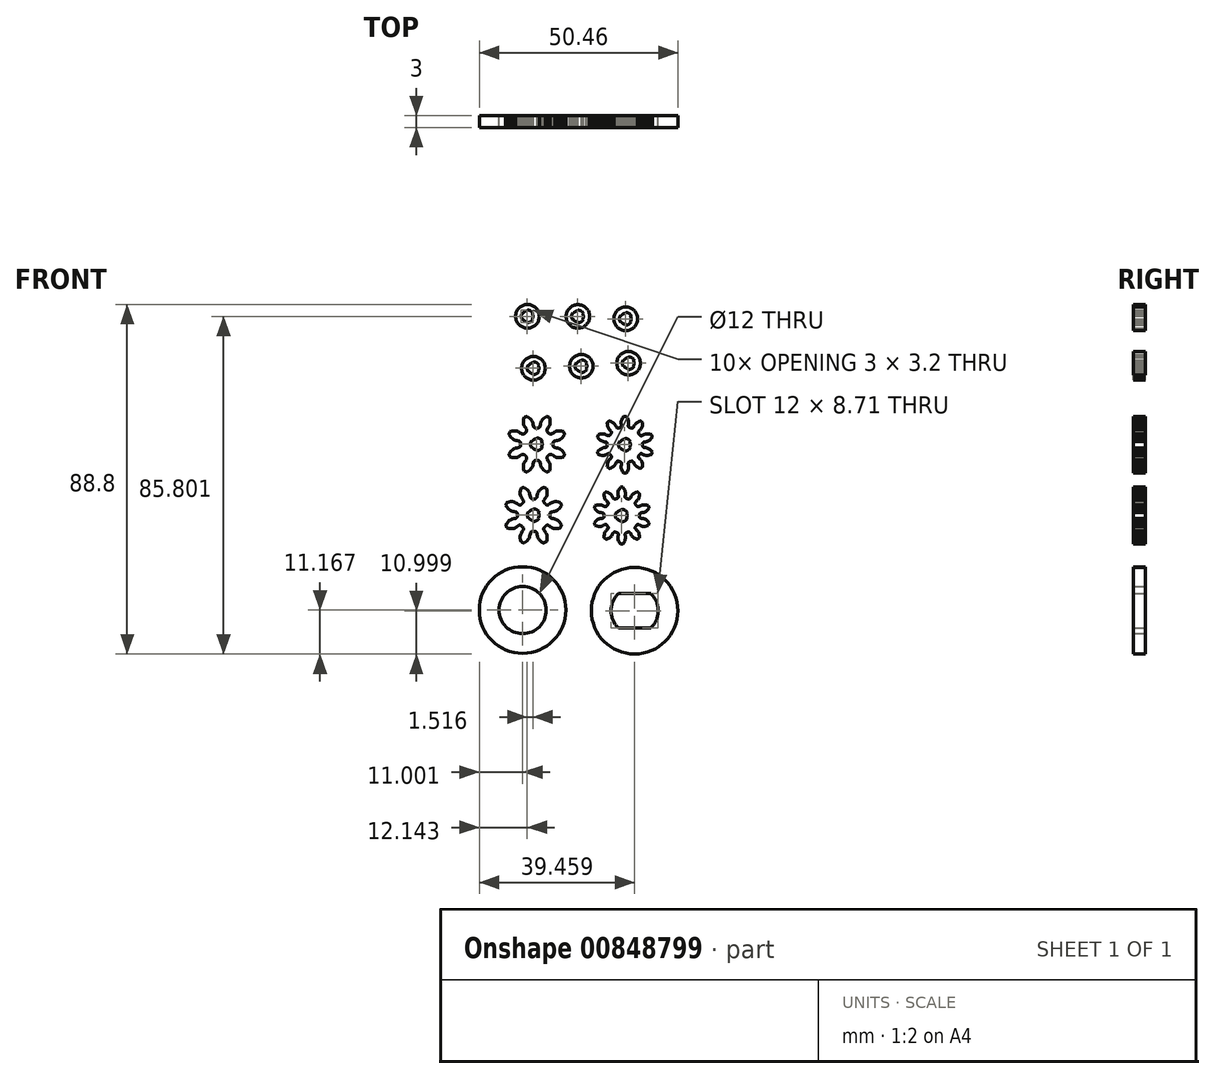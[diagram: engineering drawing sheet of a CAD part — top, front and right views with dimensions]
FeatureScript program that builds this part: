
annotation { "Feature Type Name" : "Feature", "Feature Type Description" : "" }
export const myFeature = defineFeature(function(context is Context, id is Id, definition is map)
    precondition{}
    {
        {
            var Q0;
            Q0=qCreatedBy(makeId("Front.planeOp"),FACE);
            var sketch = newSketch(context, id + "F0", { "sketchPlane" : qUnion([Q0])});
            skArc(sketch, "E0", {"start": v(10.6, 41.57) * mm, "mid": v(10.38, 40.77) * mm, "end": v(10.6, 39.97) * mm});
            skArc(sketch, "E1", {"start": v(13.36, 41.57) * mm, "mid": v(12.78, 42.16) * mm, "end": v(11.98, 42.37) * mm});
            skArc(sketch, "E2", {"start": v(13.2, 40.07) * mm, "mid": v(13.38, 40.77) * mm, "end": v(13.2, 41.47) * mm});
            skArc(sketch, "E3", {"start": v(10.77, 40.07) * mm, "mid": v(11.28, 39.56) * mm, "end": v(11.98, 39.37) * mm});
            skLineSegment(sketch, "E4", {"start": v(13.2, 41.47) * mm, "end": v(13.36, 41.57) * mm});
            skLineSegment(sketch, "E5", {"start": v(13.2, 40.07) * mm, "end": v(13.36, 39.97) * mm});
            skLineSegment(sketch, "E6", {"start": v(11.98, 39.37) * mm, "end": v(11.98, 39.17) * mm});
            skLineSegment(sketch, "E7", {"start": v(10.77, 40.07) * mm, "end": v(10.6, 39.97) * mm});
            skLineSegment(sketch, "E8", {"start": v(10.77, 41.47) * mm, "end": v(10.6, 41.57) * mm});
            skLineSegment(sketch, "E9", {"start": v(11.98, 42.17) * mm, "end": v(11.98, 42.37) * mm});
            skArc(sketch, "E10", {"start": v(11.98, 42.17) * mm, "mid": v(11.28, 41.98) * mm, "end": v(10.77, 41.47) * mm});
            skArc(sketch, "E11", {"start": v(11.98, 39.17) * mm, "mid": v(12.78, 39.38) * mm, "end": v(13.36, 39.97) * mm});
            skArc(sketch, "E12", {"start": v(-1.57, 42.17) * mm, "mid": v(-1.78, 41.37) * mm, "end": v(-1.57, 40.57) * mm});
            skArc(sketch, "E13", {"start": v(1.2, 42.17) * mm, "mid": v(0.62, 42.76) * mm, "end": v(-0.18, 42.97) * mm});
            skArc(sketch, "E14", {"start": v(1.03, 40.67) * mm, "mid": v(1.22, 41.37) * mm, "end": v(1.03, 42.07) * mm});
            skArc(sketch, "E15", {"start": v(-1.4, 40.67) * mm, "mid": v(-0.88, 40.16) * mm, "end": v(-0.18, 39.97) * mm});
            skLineSegment(sketch, "E16", {"start": v(1.03, 42.07) * mm, "end": v(1.2, 42.17) * mm});
            skLineSegment(sketch, "E17", {"start": v(1.03, 40.67) * mm, "end": v(1.2, 40.57) * mm});
            skLineSegment(sketch, "E18", {"start": v(-0.18, 39.97) * mm, "end": v(-0.18, 39.77) * mm});
            skLineSegment(sketch, "E19", {"start": v(-1.4, 40.67) * mm, "end": v(-1.57, 40.57) * mm});
            skLineSegment(sketch, "E20", {"start": v(-1.4, 42.07) * mm, "end": v(-1.57, 42.17) * mm});
            skLineSegment(sketch, "E21", {"start": v(-0.18, 42.77) * mm, "end": v(-0.18, 42.97) * mm});
            skArc(sketch, "E22", {"start": v(-0.18, 42.77) * mm, "mid": v(-0.88, 42.59) * mm, "end": v(-1.4, 42.07) * mm});
            skArc(sketch, "E23", {"start": v(-0.18, 39.77) * mm, "mid": v(0.62, 39.99) * mm, "end": v(1.2, 40.57) * mm});
            skCircle(sketch, "E24", {"center": v(-0.18, 41.37) * mm, "radius": 3 * mm});
            skArc(sketch, "E25", {"start": v(-14.37, 42.2) * mm, "mid": v(-14.59, 41.4) * mm, "end": v(-14.37, 40.6) * mm});
            skArc(sketch, "E26", {"start": v(-11.6, 42.2) * mm, "mid": v(-12.19, 42.79) * mm, "end": v(-12.99, 43) * mm});
            skArc(sketch, "E27", {"start": v(-11.77, 40.7) * mm, "mid": v(-11.59, 41.4) * mm, "end": v(-11.77, 42.1) * mm});
            skArc(sketch, "E28", {"start": v(-14.2, 40.7) * mm, "mid": v(-13.69, 40.19) * mm, "end": v(-12.99, 40) * mm});
            skLineSegment(sketch, "E29", {"start": v(-11.77, 42.1) * mm, "end": v(-11.6, 42.2) * mm});
            skLineSegment(sketch, "E30", {"start": v(-11.77, 40.7) * mm, "end": v(-11.6, 40.6) * mm});
            skLineSegment(sketch, "E31", {"start": v(-12.99, 40) * mm, "end": v(-12.99, 39.8) * mm});
            skLineSegment(sketch, "E32", {"start": v(-14.2, 40.7) * mm, "end": v(-14.37, 40.6) * mm});
            skLineSegment(sketch, "E33", {"start": v(-14.2, 42.1) * mm, "end": v(-14.37, 42.2) * mm});
            skLineSegment(sketch, "E34", {"start": v(-12.99, 42.8) * mm, "end": v(-12.99, 43) * mm});
            skArc(sketch, "E35", {"start": v(-12.99, 42.8) * mm, "mid": v(-13.69, 42.61) * mm, "end": v(-14.2, 42.1) * mm});
            skArc(sketch, "E36", {"start": v(-12.99, 39.8) * mm, "mid": v(-12.19, 40.02) * mm, "end": v(-11.6, 40.6) * mm});
            skArc(sketch, "E37", {"start": v(11.32, 30.3) * mm, "mid": v(11.1, 29.5) * mm, "end": v(11.32, 28.7) * mm});
            skArc(sketch, "E38", {"start": v(14.1, 30.3) * mm, "mid": v(13.5, 30.88) * mm, "end": v(12.7, 31.1) * mm});
            skArc(sketch, "E39", {"start": v(13.92, 28.8) * mm, "mid": v(14.1, 29.5) * mm, "end": v(13.92, 30.2) * mm});
            skArc(sketch, "E40", {"start": v(11.5, 28.8) * mm, "mid": v(12, 28.28) * mm, "end": v(12.7, 28.1) * mm});
            skLineSegment(sketch, "E41", {"start": v(13.92, 30.2) * mm, "end": v(14.1, 30.3) * mm});
            skLineSegment(sketch, "E42", {"start": v(13.92, 28.8) * mm, "end": v(14.1, 28.7) * mm});
            skLineSegment(sketch, "E43", {"start": v(12.7, 28.1) * mm, "end": v(12.7, 27.9) * mm});
            skLineSegment(sketch, "E44", {"start": v(11.5, 28.8) * mm, "end": v(11.32, 28.7) * mm});
            skLineSegment(sketch, "E45", {"start": v(11.5, 30.2) * mm, "end": v(11.32, 30.3) * mm});
            skLineSegment(sketch, "E46", {"start": v(12.7, 30.9) * mm, "end": v(12.7, 31.1) * mm});
            skArc(sketch, "E47", {"start": v(12.7, 30.9) * mm, "mid": v(12, 30.7) * mm, "end": v(11.5, 30.2) * mm});
            skArc(sketch, "E48", {"start": v(12.7, 27.9) * mm, "mid": v(13.5, 28.1) * mm, "end": v(14.1, 28.7) * mm});
            skCircle(sketch, "E49", {"center": v(12.7, 29.5) * mm, "radius": 3 * mm});
            skArc(sketch, "E50", {"start": v(-0.68, 29.53) * mm, "mid": v(-0.9, 28.73) * mm, "end": v(-0.68, 27.93) * mm});
            skArc(sketch, "E51", {"start": v(2.09, 29.53) * mm, "mid": v(1.5, 30.11) * mm, "end": v(0.7, 30.33) * mm});
            skArc(sketch, "E52", {"start": v(1.92, 28.03) * mm, "mid": v(2.1, 28.73) * mm, "end": v(1.92, 29.43) * mm});
            skArc(sketch, "E53", {"start": v(-0.5, 28.03) * mm, "mid": v(0, 27.51) * mm, "end": v(0.7, 27.33) * mm});
            skLineSegment(sketch, "E54", {"start": v(1.92, 29.43) * mm, "end": v(2.09, 29.53) * mm});
            skLineSegment(sketch, "E55", {"start": v(1.92, 28.03) * mm, "end": v(2.09, 27.93) * mm});
            skLineSegment(sketch, "E56", {"start": v(0.7, 27.33) * mm, "end": v(0.7, 27.13) * mm});
            skLineSegment(sketch, "E57", {"start": v(-0.5, 28.03) * mm, "end": v(-0.68, 27.93) * mm});
            skLineSegment(sketch, "E58", {"start": v(-0.5, 29.43) * mm, "end": v(-0.68, 29.53) * mm});
            skLineSegment(sketch, "E59", {"start": v(0.7, 30.13) * mm, "end": v(0.7, 30.33) * mm});
            skArc(sketch, "E60", {"start": v(0.7, 30.13) * mm, "mid": v(0, 29.94) * mm, "end": v(-0.5, 29.43) * mm});
            skArc(sketch, "E61", {"start": v(0.7, 27.13) * mm, "mid": v(1.5, 27.34) * mm, "end": v(2.09, 27.93) * mm});
            skArc(sketch, "E62", {"start": v(-12.86, 29.01) * mm, "mid": v(-13.07, 28.21) * mm, "end": v(-12.86, 27.41) * mm});
            skArc(sketch, "E63", {"start": v(-10.08, 29.01) * mm, "mid": v(-10.67, 29.6) * mm, "end": v(-11.47, 29.81) * mm});
            skArc(sketch, "E64", {"start": v(-10.26, 27.51) * mm, "mid": v(-10.07, 28.21) * mm, "end": v(-10.26, 28.91) * mm});
            skArc(sketch, "E65", {"start": v(-12.68, 27.51) * mm, "mid": v(-12.17, 27) * mm, "end": v(-11.47, 26.81) * mm});
            skLineSegment(sketch, "E66", {"start": v(-10.26, 28.91) * mm, "end": v(-10.08, 29.01) * mm});
            skLineSegment(sketch, "E67", {"start": v(-10.26, 27.51) * mm, "end": v(-10.08, 27.41) * mm});
            skLineSegment(sketch, "E68", {"start": v(-11.47, 26.81) * mm, "end": v(-11.47, 26.61) * mm});
            skLineSegment(sketch, "E69", {"start": v(-12.68, 27.51) * mm, "end": v(-12.86, 27.41) * mm});
            skLineSegment(sketch, "E70", {"start": v(-12.68, 28.91) * mm, "end": v(-12.86, 29.01) * mm});
            skLineSegment(sketch, "E71", {"start": v(-11.47, 29.61) * mm, "end": v(-11.47, 29.81) * mm});
            skArc(sketch, "E72", {"start": v(-11.47, 29.61) * mm, "mid": v(-12.17, 29.42) * mm, "end": v(-12.68, 28.91) * mm});
            skArc(sketch, "E73", {"start": v(-11.47, 26.61) * mm, "mid": v(-10.67, 26.83) * mm, "end": v(-10.08, 27.41) * mm});
            skArc(sketch, "E74", {"start": v(10.1, -29.05) * mm, "mid": v(8.23, -33.4) * mm, "end": v(10.1, -37.75) * mm});
            skLineSegment(sketch, "E75", {"start": v(18.36, -29.05) * mm, "end": v(10.1, -29.05) * mm});
            skLineSegment(sketch, "E76", {"start": v(18.36, -37.75) * mm, "end": v(10.1, -37.75) * mm});
            skCircle(sketch, "E77", {"center": v(14.23, -33.4) * mm, "radius": 11 * mm});
            skArc(sketch, "E78", {"start": v(18.36, -37.75) * mm, "mid": v(20.23, -33.4) * mm, "end": v(18.36, -29.05) * mm});
            skCircle(sketch, "E79", {"center": v(-14.23, -33.23) * mm, "radius": 6 * mm});
            skArc(sketch, "E80", {"start": v(9.57, -8.42) * mm, "mid": v(9.35, -9.22) * mm, "end": v(9.57, -10.02) * mm});
            skArc(sketch, "E81", {"start": v(12.34, -8.42) * mm, "mid": v(11.75, -7.84) * mm, "end": v(10.95, -7.62) * mm});
            skArc(sketch, "E82", {"start": v(12.17, -9.92) * mm, "mid": v(12.35, -9.22) * mm, "end": v(12.17, -8.52) * mm});
            skArc(sketch, "E83", {"start": v(9.74, -9.92) * mm, "mid": v(10.25, -10.43) * mm, "end": v(10.95, -10.62) * mm});
            skLineSegment(sketch, "E84", {"start": v(12.17, -8.52) * mm, "end": v(12.34, -8.42) * mm});
            skLineSegment(sketch, "E85", {"start": v(12.17, -9.92) * mm, "end": v(12.34, -10.02) * mm});
            skLineSegment(sketch, "E86", {"start": v(10.95, -10.62) * mm, "end": v(10.95, -10.82) * mm});
            skLineSegment(sketch, "E87", {"start": v(9.74, -9.92) * mm, "end": v(9.57, -10.02) * mm});
            skLineSegment(sketch, "E88", {"start": v(9.74, -8.52) * mm, "end": v(9.57, -8.42) * mm});
            skLineSegment(sketch, "E89", {"start": v(10.95, -7.82) * mm, "end": v(10.95, -7.62) * mm});
            skArc(sketch, "E90", {"start": v(10.95, -7.82) * mm, "mid": v(10.25, -8) * mm, "end": v(9.74, -8.52) * mm});
            skArc(sketch, "E91", {"start": v(10.95, -10.82) * mm, "mid": v(11.75, -10.6) * mm, "end": v(12.34, -10.02) * mm});
            skArc(sketch, "E92", {"start": v(-12.82, -8.3) * mm, "mid": v(-13.03, -9.1) * mm, "end": v(-12.82, -9.9) * mm});
            skArc(sketch, "E93", {"start": v(-10.05, -8.3) * mm, "mid": v(-10.63, -7.72) * mm, "end": v(-11.43, -7.5) * mm});
            skArc(sketch, "E94", {"start": v(-10.22, -9.8) * mm, "mid": v(-10.03, -9.1) * mm, "end": v(-10.22, -8.4) * mm});
            skArc(sketch, "E95", {"start": v(-12.65, -9.8) * mm, "mid": v(-12.13, -10.32) * mm, "end": v(-11.43, -10.5) * mm});
            skLineSegment(sketch, "E96", {"start": v(-10.22, -8.4) * mm, "end": v(-10.05, -8.3) * mm});
            skLineSegment(sketch, "E97", {"start": v(-10.22, -9.8) * mm, "end": v(-10.05, -9.9) * mm});
            skLineSegment(sketch, "E98", {"start": v(-11.43, -10.5) * mm, "end": v(-11.43, -10.7) * mm});
            skLineSegment(sketch, "E99", {"start": v(-12.65, -9.8) * mm, "end": v(-12.82, -9.9) * mm});
            skLineSegment(sketch, "E100", {"start": v(-12.65, -8.4) * mm, "end": v(-12.82, -8.3) * mm});
            skLineSegment(sketch, "E101", {"start": v(-11.43, -7.7) * mm, "end": v(-11.43, -7.5) * mm});
            skArc(sketch, "E102", {"start": v(-11.43, -7.7) * mm, "mid": v(-12.13, -7.9) * mm, "end": v(-12.65, -8.4) * mm});
            skArc(sketch, "E103", {"start": v(-11.43, -10.7) * mm, "mid": v(-10.63, -10.49) * mm, "end": v(-10.05, -9.9) * mm});
            skArc(sketch, "E104", {"start": v(12.53, -5) * mm, "mid": v(12.34, -4.94) * mm, "end": v(12.16, -4.89) * mm});
            skArc(sketch, "E105", {"start": v(12.53, -5) * mm, "mid": v(12.88, -5) * mm, "end": v(13.14, -4.76) * mm});
            skLineSegment(sketch, "E106", {"start": v(14.48, -3.36) * mm, "end": v(14.9, -3.2) * mm});
            skLineSegment(sketch, "E107", {"start": v(14.1, -3.55) * mm, "end": v(14.48, -3.36) * mm});
            skLineSegment(sketch, "E108", {"start": v(13.85, -3.73) * mm, "end": v(14.1, -3.55) * mm});
            skLineSegment(sketch, "E109", {"start": v(13.63, -3.92) * mm, "end": v(13.85, -3.73) * mm});
            skLineSegment(sketch, "E110", {"start": v(13.49, -4.09) * mm, "end": v(13.63, -3.92) * mm});
            skLineSegment(sketch, "E111", {"start": v(13.45, -4.14) * mm, "end": v(13.49, -4.09) * mm});
            skLineSegment(sketch, "E112", {"start": v(13.42, -4.2) * mm, "end": v(13.45, -4.14) * mm});
            skLineSegment(sketch, "E113", {"start": v(13.37, -4.3) * mm, "end": v(13.42, -4.2) * mm});
            skLineSegment(sketch, "E114", {"start": v(13.27, -4.5) * mm, "end": v(13.37, -4.3) * mm});
            skLineSegment(sketch, "E115", {"start": v(13.14, -4.76) * mm, "end": v(13.27, -4.5) * mm});
            skArc(sketch, "E116", {"start": v(15.47, -3.61) * mm, "mid": v(15.19, -3.4) * mm, "end": v(14.9, -3.2) * mm});
            skLineSegment(sketch, "E117", {"start": v(15.44, -4.06) * mm, "end": v(15.47, -3.61) * mm});
            skLineSegment(sketch, "E118", {"start": v(15.37, -4.47) * mm, "end": v(15.44, -4.06) * mm});
            skLineSegment(sketch, "E119", {"start": v(15.28, -4.78) * mm, "end": v(15.37, -4.47) * mm});
            skLineSegment(sketch, "E120", {"start": v(15.17, -5.03) * mm, "end": v(15.28, -4.78) * mm});
            skLineSegment(sketch, "E121", {"start": v(15.05, -5.23) * mm, "end": v(15.17, -5.03) * mm});
            skLineSegment(sketch, "E122", {"start": v(15.01, -5.28) * mm, "end": v(15.05, -5.23) * mm});
            skLineSegment(sketch, "E123", {"start": v(14.98, -5.32) * mm, "end": v(15.01, -5.28) * mm});
            skLineSegment(sketch, "E124", {"start": v(14.9, -5.4) * mm, "end": v(14.98, -5.32) * mm});
            skLineSegment(sketch, "E125", {"start": v(14.73, -5.56) * mm, "end": v(14.9, -5.4) * mm});
            skLineSegment(sketch, "E126", {"start": v(14.52, -5.76) * mm, "end": v(14.73, -5.56) * mm});
            skArc(sketch, "E127", {"start": v(14.52, -5.76) * mm, "mid": v(14.37, -6.08) * mm, "end": v(14.48, -6.42) * mm});
            skArc(sketch, "E128", {"start": v(14.7, -6.74) * mm, "mid": v(14.6, -6.58) * mm, "end": v(14.48, -6.42) * mm});
            skArc(sketch, "E129", {"start": v(14.7, -6.74) * mm, "mid": v(15, -6.94) * mm, "end": v(15.35, -6.9) * mm});
            skLineSegment(sketch, "E130", {"start": v(17.25, -6.55) * mm, "end": v(17.68, -6.66) * mm});
            skLineSegment(sketch, "E131", {"start": v(16.84, -6.5) * mm, "end": v(17.25, -6.55) * mm});
            skCircle(sketch, "E132", {"center": v(11.98, 40.77) * mm, "radius": 3 * mm});
            skLineSegment(sketch, "E133", {"start": v(16.52, -6.48) * mm, "end": v(16.84, -6.5) * mm});
            skLineSegment(sketch, "E134", {"start": v(16.24, -6.5) * mm, "end": v(16.52, -6.48) * mm});
            skLineSegment(sketch, "E135", {"start": v(16.02, -6.56) * mm, "end": v(16.24, -6.5) * mm});
            skLineSegment(sketch, "E136", {"start": v(15.96, -6.58) * mm, "end": v(16.02, -6.56) * mm});
            skLineSegment(sketch, "E137", {"start": v(15.9, -6.6) * mm, "end": v(15.96, -6.58) * mm});
            skLineSegment(sketch, "E138", {"start": v(15.8, -6.66) * mm, "end": v(15.9, -6.6) * mm});
            skLineSegment(sketch, "E139", {"start": v(15.6, -6.76) * mm, "end": v(15.8, -6.66) * mm});
            skLineSegment(sketch, "E140", {"start": v(15.35, -6.9) * mm, "end": v(15.6, -6.76) * mm});
            skArc(sketch, "E141", {"start": v(17.9, -7.33) * mm, "mid": v(17.8, -7) * mm, "end": v(17.68, -6.66) * mm});
            skLineSegment(sketch, "E142", {"start": v(17.62, -7.68) * mm, "end": v(17.9, -7.33) * mm});
            skLineSegment(sketch, "E143", {"start": v(17.32, -7.97) * mm, "end": v(17.62, -7.68) * mm});
            skLineSegment(sketch, "E144", {"start": v(17.07, -8.17) * mm, "end": v(17.32, -7.97) * mm});
            skLineSegment(sketch, "E145", {"start": v(16.83, -8.31) * mm, "end": v(17.07, -8.17) * mm});
            skLineSegment(sketch, "E146", {"start": v(16.62, -8.4) * mm, "end": v(16.83, -8.31) * mm});
            skLineSegment(sketch, "E147", {"start": v(16.55, -8.42) * mm, "end": v(16.62, -8.4) * mm});
            skLineSegment(sketch, "E148", {"start": v(16.5, -8.43) * mm, "end": v(16.55, -8.42) * mm});
            skLineSegment(sketch, "E149", {"start": v(16.38, -8.45) * mm, "end": v(16.5, -8.43) * mm});
            skLineSegment(sketch, "E150", {"start": v(16.16, -8.48) * mm, "end": v(16.38, -8.45) * mm});
            skLineSegment(sketch, "E151", {"start": v(15.87, -8.52) * mm, "end": v(16.16, -8.48) * mm});
            skArc(sketch, "E152", {"start": v(15.87, -8.52) * mm, "mid": v(15.56, -8.7) * mm, "end": v(15.45, -9.03) * mm});
            skArc(sketch, "E153", {"start": v(15.45, -9.41) * mm, "mid": v(15.45, -9.22) * mm, "end": v(15.45, -9.03) * mm});
            skArc(sketch, "E154", {"start": v(15.45, -9.41) * mm, "mid": v(15.56, -9.75) * mm, "end": v(15.87, -9.92) * mm});
            skLineSegment(sketch, "E155", {"start": v(17.62, -10.76) * mm, "end": v(17.9, -11.1) * mm});
            skLineSegment(sketch, "E156", {"start": v(17.32, -10.47) * mm, "end": v(17.62, -10.76) * mm});
            skLineSegment(sketch, "E157", {"start": v(17.07, -10.28) * mm, "end": v(17.32, -10.47) * mm});
            skLineSegment(sketch, "E158", {"start": v(16.83, -10.13) * mm, "end": v(17.07, -10.28) * mm});
            skLineSegment(sketch, "E159", {"start": v(16.62, -10.04) * mm, "end": v(16.83, -10.13) * mm});
            skLineSegment(sketch, "E160", {"start": v(16.55, -10.02) * mm, "end": v(16.62, -10.04) * mm});
            skLineSegment(sketch, "E161", {"start": v(16.5, -10.02) * mm, "end": v(16.55, -10.02) * mm});
            skLineSegment(sketch, "E162", {"start": v(16.38, -10) * mm, "end": v(16.5, -10.02) * mm});
            skLineSegment(sketch, "E163", {"start": v(16.16, -9.97) * mm, "end": v(16.38, -10) * mm});
            skLineSegment(sketch, "E164", {"start": v(15.87, -9.92) * mm, "end": v(16.16, -9.97) * mm});
            skArc(sketch, "E165", {"start": v(17.68, -11.78) * mm, "mid": v(17.8, -11.45) * mm, "end": v(17.9, -11.1) * mm});
            skLineSegment(sketch, "E166", {"start": v(17.25, -11.9) * mm, "end": v(17.68, -11.78) * mm});
            skLineSegment(sketch, "E167", {"start": v(16.84, -11.95) * mm, "end": v(17.25, -11.9) * mm});
            skLineSegment(sketch, "E168", {"start": v(16.52, -11.96) * mm, "end": v(16.84, -11.95) * mm});
            skLineSegment(sketch, "E169", {"start": v(16.24, -11.94) * mm, "end": v(16.52, -11.96) * mm});
            skLineSegment(sketch, "E170", {"start": v(16.02, -11.89) * mm, "end": v(16.24, -11.94) * mm});
            skLineSegment(sketch, "E171", {"start": v(15.96, -11.86) * mm, "end": v(16.02, -11.89) * mm});
            skLineSegment(sketch, "E172", {"start": v(15.9, -11.84) * mm, "end": v(15.96, -11.86) * mm});
            skLineSegment(sketch, "E173", {"start": v(15.8, -11.79) * mm, "end": v(15.9, -11.84) * mm});
            skLineSegment(sketch, "E174", {"start": v(15.6, -11.68) * mm, "end": v(15.8, -11.79) * mm});
            skLineSegment(sketch, "E175", {"start": v(15.35, -11.55) * mm, "end": v(15.6, -11.68) * mm});
            skArc(sketch, "E176", {"start": v(15.35, -11.55) * mm, "mid": v(15, -11.5) * mm, "end": v(14.7, -11.7) * mm});
            skArc(sketch, "E177", {"start": v(14.48, -12.02) * mm, "mid": v(14.6, -11.87) * mm, "end": v(14.7, -11.7) * mm});
            skArc(sketch, "E178", {"start": v(14.48, -12.02) * mm, "mid": v(14.37, -12.36) * mm, "end": v(14.52, -12.68) * mm});
            skLineSegment(sketch, "E179", {"start": v(15.44, -14.38) * mm, "end": v(15.47, -14.83) * mm});
            skLineSegment(sketch, "E180", {"start": v(15.37, -13.97) * mm, "end": v(15.44, -14.38) * mm});
            skLineSegment(sketch, "E181", {"start": v(15.28, -13.67) * mm, "end": v(15.37, -13.97) * mm});
            skLineSegment(sketch, "E182", {"start": v(15.17, -13.4) * mm, "end": v(15.28, -13.67) * mm});
            skLineSegment(sketch, "E183", {"start": v(15.05, -13.22) * mm, "end": v(15.17, -13.4) * mm});
            skLineSegment(sketch, "E184", {"start": v(15.01, -13.16) * mm, "end": v(15.05, -13.22) * mm});
            skLineSegment(sketch, "E185", {"start": v(14.98, -13.12) * mm, "end": v(15.01, -13.16) * mm});
            skLineSegment(sketch, "E186", {"start": v(14.9, -13.04) * mm, "end": v(14.98, -13.12) * mm});
            skLineSegment(sketch, "E187", {"start": v(14.73, -12.88) * mm, "end": v(14.9, -13.04) * mm});
            skLineSegment(sketch, "E188", {"start": v(14.52, -12.68) * mm, "end": v(14.73, -12.88) * mm});
            skArc(sketch, "E189", {"start": v(14.9, -15.25) * mm, "mid": v(15.19, -15.05) * mm, "end": v(15.47, -14.83) * mm});
            skLineSegment(sketch, "E190", {"start": v(14.48, -15.08) * mm, "end": v(14.9, -15.25) * mm});
            skLineSegment(sketch, "E191", {"start": v(14.1, -14.89) * mm, "end": v(14.48, -15.08) * mm});
            skLineSegment(sketch, "E192", {"start": v(13.85, -14.7) * mm, "end": v(14.1, -14.89) * mm});
            skLineSegment(sketch, "E193", {"start": v(13.63, -14.53) * mm, "end": v(13.85, -14.7) * mm});
            skLineSegment(sketch, "E194", {"start": v(13.49, -14.36) * mm, "end": v(13.63, -14.53) * mm});
            skLineSegment(sketch, "E195", {"start": v(13.45, -14.3) * mm, "end": v(13.49, -14.36) * mm});
            skLineSegment(sketch, "E196", {"start": v(13.42, -14.25) * mm, "end": v(13.45, -14.3) * mm});
            skLineSegment(sketch, "E197", {"start": v(13.37, -14.15) * mm, "end": v(13.42, -14.25) * mm});
            skLineSegment(sketch, "E198", {"start": v(13.27, -13.94) * mm, "end": v(13.37, -14.15) * mm});
            skLineSegment(sketch, "E199", {"start": v(13.14, -13.68) * mm, "end": v(13.27, -13.94) * mm});
            skArc(sketch, "E200", {"start": v(13.14, -13.68) * mm, "mid": v(12.88, -13.44) * mm, "end": v(12.53, -13.44) * mm});
            skArc(sketch, "E201", {"start": v(12.16, -13.56) * mm, "mid": v(12.34, -13.5) * mm, "end": v(12.53, -13.44) * mm});
            skArc(sketch, "E202", {"start": v(12.16, -13.56) * mm, "mid": v(11.87, -13.77) * mm, "end": v(11.8, -14.12) * mm});
            skLineSegment(sketch, "E203", {"start": v(-4.97, 7.85) * mm, "end": v(-4.7, 7.71) * mm});
            skLineSegment(sketch, "E204", {"start": v(-4.7, 7.71) * mm, "end": v(-4.4, 7.5) * mm});
            skLineSegment(sketch, "E205", {"start": v(-4.4, 7.5) * mm, "end": v(-4.1, 7.2) * mm});
            skLineSegment(sketch, "E206", {"start": v(-4.1, 7.2) * mm, "end": v(-3.82, 6.83) * mm});
            skLineSegment(sketch, "E207", {"start": v(-3.82, 6.83) * mm, "end": v(-3.55, 6.41) * mm});
            skArc(sketch, "E208", {"start": v(-6.5, 8.69) * mm, "mid": v(-6.38, 8.28) * mm, "end": v(-6, 8.06) * mm});
            skArc(sketch, "E209", {"start": v(-6.5, 8.69) * mm, "mid": v(-6.5, 8.9) * mm, "end": v(-6.5, 9.12) * mm});
            skArc(sketch, "E210", {"start": v(-6, 9.75) * mm, "mid": v(-6.38, 9.53) * mm, "end": v(-6.5, 9.12) * mm});
            skLineSegment(sketch, "E211", {"start": v(-6, 9.75) * mm, "end": v(-5.6, 9.83) * mm});
            skLineSegment(sketch, "E212", {"start": v(-5.6, 9.83) * mm, "end": v(-5.27, 9.89) * mm});
            skLineSegment(sketch, "E213", {"start": v(-5.27, 9.89) * mm, "end": v(-5.11, 9.92) * mm});
            skLineSegment(sketch, "E214", {"start": v(-5.11, 9.92) * mm, "end": v(-5.05, 9.93) * mm});
            skLineSegment(sketch, "E215", {"start": v(-5.05, 9.93) * mm, "end": v(-5.02, 9.94) * mm});
            skLineSegment(sketch, "E216", {"start": v(-5.02, 9.94) * mm, "end": v(-4.97, 9.96) * mm});
            skLineSegment(sketch, "E217", {"start": v(-4.97, 9.96) * mm, "end": v(-4.7, 10.1) * mm});
            skLineSegment(sketch, "E218", {"start": v(-4.7, 10.1) * mm, "end": v(-4.4, 10.32) * mm});
            skLineSegment(sketch, "E219", {"start": v(-4.4, 10.32) * mm, "end": v(-4.1, 10.61) * mm});
            skLineSegment(sketch, "E220", {"start": v(-4.1, 10.61) * mm, "end": v(-3.82, 10.97) * mm});
            skLineSegment(sketch, "E221", {"start": v(-3.82, 10.97) * mm, "end": v(-3.55, 11.4) * mm});
            skArc(sketch, "E222", {"start": v(-3.55, 11.4) * mm, "mid": v(-3.7, 11.77) * mm, "end": v(-3.86, 12.14) * mm});
            skLineSegment(sketch, "E223", {"start": v(-6.76, 11.57) * mm, "end": v(-6.41, 11.81) * mm});
            skLineSegment(sketch, "E224", {"start": v(-6.41, 11.81) * mm, "end": v(-6.14, 12) * mm});
            skLineSegment(sketch, "E225", {"start": v(-6.14, 12) * mm, "end": v(-6.01, 12.09) * mm});
            skLineSegment(sketch, "E226", {"start": v(-6.01, 12.09) * mm, "end": v(-5.96, 12.12) * mm});
            skLineSegment(sketch, "E227", {"start": v(-5.96, 12.12) * mm, "end": v(-5.93, 12.14) * mm});
            skLineSegment(sketch, "E228", {"start": v(-5.93, 12.14) * mm, "end": v(-5.88, 12.16) * mm});
            skLineSegment(sketch, "E229", {"start": v(-5.88, 12.16) * mm, "end": v(-5.6, 12.25) * mm});
            skLineSegment(sketch, "E230", {"start": v(-5.6, 12.25) * mm, "end": v(-5.23, 12.3) * mm});
            skLineSegment(sketch, "E231", {"start": v(-5.23, 12.3) * mm, "end": v(-4.8, 12.3) * mm});
            skLineSegment(sketch, "E232", {"start": v(-4.8, 12.3) * mm, "end": v(-4.35, 12.25) * mm});
            skLineSegment(sketch, "E233", {"start": v(-4.35, 12.25) * mm, "end": v(-3.86, 12.14) * mm});
            skArc(sketch, "E234", {"start": v(-7.56, 11.66) * mm, "mid": v(-7.18, 11.47) * mm, "end": v(-6.76, 11.57) * mm});
            skArc(sketch, "E235", {"start": v(-7.56, 11.66) * mm, "mid": v(-7.7, 11.82) * mm, "end": v(-7.87, 11.97) * mm});
            skArc(sketch, "E236", {"start": v(-7.96, 12.76) * mm, "mid": v(-8.06, 12.35) * mm, "end": v(-7.87, 11.97) * mm});
            skLineSegment(sketch, "E237", {"start": v(-7.96, 12.76) * mm, "end": v(-7.72, 13.12) * mm});
            skLineSegment(sketch, "E238", {"start": v(-7.72, 13.12) * mm, "end": v(-7.53, 13.39) * mm});
            skLineSegment(sketch, "E239", {"start": v(-7.53, 13.39) * mm, "end": v(-7.44, 13.52) * mm});
            skLineSegment(sketch, "E240", {"start": v(-7.44, 13.52) * mm, "end": v(-7.4, 13.57) * mm});
            skLineSegment(sketch, "E241", {"start": v(-7.4, 13.57) * mm, "end": v(-7.4, 13.6) * mm});
            skLineSegment(sketch, "E242", {"start": v(-7.4, 13.6) * mm, "end": v(-7.37, 13.65) * mm});
            skLineSegment(sketch, "E243", {"start": v(-7.37, 13.65) * mm, "end": v(-7.28, 13.93) * mm});
            skLineSegment(sketch, "E244", {"start": v(-7.28, 13.93) * mm, "end": v(-7.23, 14.3) * mm});
            skLineSegment(sketch, "E245", {"start": v(-7.23, 14.3) * mm, "end": v(-7.22, 14.72) * mm});
            skLineSegment(sketch, "E246", {"start": v(-7.22, 14.72) * mm, "end": v(-7.27, 15.18) * mm});
            skLineSegment(sketch, "E247", {"start": v(-7.27, 15.18) * mm, "end": v(-7.38, 15.67) * mm});
            skArc(sketch, "E248", {"start": v(-7.38, 15.67) * mm, "mid": v(-7.75, 15.83) * mm, "end": v(-8.13, 15.98) * mm});
            skLineSegment(sketch, "E249", {"start": v(-9.78, 13.52) * mm, "end": v(-9.7, 13.94) * mm});
            skLineSegment(sketch, "E250", {"start": v(-9.7, 13.94) * mm, "end": v(-9.64, 14.26) * mm});
            skLineSegment(sketch, "E251", {"start": v(-9.64, 14.26) * mm, "end": v(-9.61, 14.42) * mm});
            skLineSegment(sketch, "E252", {"start": v(-9.61, 14.42) * mm, "end": v(-9.6, 14.47) * mm});
            skLineSegment(sketch, "E253", {"start": v(-9.6, 14.47) * mm, "end": v(-9.59, 14.51) * mm});
            skLineSegment(sketch, "E254", {"start": v(-9.59, 14.51) * mm, "end": v(-9.57, 14.56) * mm});
            skLineSegment(sketch, "E255", {"start": v(-9.57, 14.56) * mm, "end": v(-9.43, 14.82) * mm});
            skLineSegment(sketch, "E256", {"start": v(-9.43, 14.82) * mm, "end": v(-9.21, 15.12) * mm});
            skLineSegment(sketch, "E257", {"start": v(-9.21, 15.12) * mm, "end": v(-8.92, 15.42) * mm});
            skLineSegment(sketch, "E258", {"start": v(-8.92, 15.42) * mm, "end": v(-8.55, 15.71) * mm});
            skLineSegment(sketch, "E259", {"start": v(-8.55, 15.71) * mm, "end": v(-8.13, 15.98) * mm});
            skArc(sketch, "E260", {"start": v(-10.4, 13.02) * mm, "mid": v(-10, 13.15) * mm, "end": v(-9.78, 13.52) * mm});
            skArc(sketch, "E261", {"start": v(-10.4, 13.02) * mm, "mid": v(-10.62, 13.03) * mm, "end": v(-10.84, 13.02) * mm});
            skArc(sketch, "E262", {"start": v(-11.47, 13.52) * mm, "mid": v(-11.25, 13.15) * mm, "end": v(-10.84, 13.02) * mm});
            skLineSegment(sketch, "E263", {"start": v(-11.47, 13.52) * mm, "end": v(-11.55, 13.94) * mm});
            skLineSegment(sketch, "E264", {"start": v(-11.55, 13.94) * mm, "end": v(-11.6, 14.26) * mm});
            skLineSegment(sketch, "E265", {"start": v(-11.6, 14.26) * mm, "end": v(-11.64, 14.42) * mm});
            skLineSegment(sketch, "E266", {"start": v(-11.64, 14.42) * mm, "end": v(-11.65, 14.47) * mm});
            skLineSegment(sketch, "E267", {"start": v(-11.65, 14.47) * mm, "end": v(-11.66, 14.51) * mm});
            skLineSegment(sketch, "E268", {"start": v(-11.66, 14.51) * mm, "end": v(-11.68, 14.56) * mm});
            skCircle(sketch, "E269", {"center": v(0.7, 28.73) * mm, "radius": 3 * mm});
            skLineSegment(sketch, "E270", {"start": v(-11.68, 14.56) * mm, "end": v(-11.82, 14.82) * mm});
            skLineSegment(sketch, "E271", {"start": v(-11.82, 14.82) * mm, "end": v(-12.04, 15.12) * mm});
            skLineSegment(sketch, "E272", {"start": v(-12.04, 15.12) * mm, "end": v(-12.33, 15.42) * mm});
            skLineSegment(sketch, "E273", {"start": v(-12.33, 15.42) * mm, "end": v(-12.7, 15.71) * mm});
            skLineSegment(sketch, "E274", {"start": v(-12.7, 15.71) * mm, "end": v(-13.12, 15.98) * mm});
            skArc(sketch, "E275", {"start": v(-13.12, 15.98) * mm, "mid": v(-13.5, 15.83) * mm, "end": v(-13.86, 15.67) * mm});
            skLineSegment(sketch, "E276", {"start": v(-13.29, 12.76) * mm, "end": v(-13.53, 13.12) * mm});
            skLineSegment(sketch, "E277", {"start": v(-13.53, 13.12) * mm, "end": v(-13.72, 13.39) * mm});
            skLineSegment(sketch, "E278", {"start": v(-13.72, 13.39) * mm, "end": v(-13.8, 13.52) * mm});
            skLineSegment(sketch, "E279", {"start": v(-13.8, 13.52) * mm, "end": v(-13.84, 13.57) * mm});
            skLineSegment(sketch, "E280", {"start": v(-13.84, 13.57) * mm, "end": v(-13.86, 13.6) * mm});
            skLineSegment(sketch, "E281", {"start": v(-13.86, 13.6) * mm, "end": v(-13.88, 13.65) * mm});
            skLineSegment(sketch, "E282", {"start": v(-13.88, 13.65) * mm, "end": v(-13.97, 13.93) * mm});
            skLineSegment(sketch, "E283", {"start": v(-13.97, 13.93) * mm, "end": v(-14.02, 14.3) * mm});
            skLineSegment(sketch, "E284", {"start": v(-14.02, 14.3) * mm, "end": v(-14.03, 14.72) * mm});
            skLineSegment(sketch, "E285", {"start": v(-14.03, 14.72) * mm, "end": v(-13.97, 15.18) * mm});
            skLineSegment(sketch, "E286", {"start": v(-13.97, 15.18) * mm, "end": v(-13.86, 15.67) * mm});
            skArc(sketch, "E287", {"start": v(-13.38, 11.97) * mm, "mid": v(-13.19, 12.35) * mm, "end": v(-13.29, 12.76) * mm});
            skArc(sketch, "E288", {"start": v(-13.38, 11.97) * mm, "mid": v(-13.54, 11.82) * mm, "end": v(-13.7, 11.66) * mm});
            skArc(sketch, "E289", {"start": v(-14.49, 11.57) * mm, "mid": v(-14.07, 11.47) * mm, "end": v(-13.7, 11.66) * mm});
            skLineSegment(sketch, "E290", {"start": v(-14.49, 11.57) * mm, "end": v(-14.84, 11.81) * mm});
            skLineSegment(sketch, "E291", {"start": v(-14.84, 11.81) * mm, "end": v(-15.1, 12) * mm});
            skLineSegment(sketch, "E292", {"start": v(-15.1, 12) * mm, "end": v(-15.24, 12.09) * mm});
            skLineSegment(sketch, "E293", {"start": v(-15.24, 12.09) * mm, "end": v(-15.29, 12.12) * mm});
            skLineSegment(sketch, "E294", {"start": v(-15.29, 12.12) * mm, "end": v(-15.32, 12.14) * mm});
            skLineSegment(sketch, "E295", {"start": v(-15.32, 12.14) * mm, "end": v(-15.37, 12.16) * mm});
            skLineSegment(sketch, "E296", {"start": v(-15.37, 12.16) * mm, "end": v(-15.65, 12.25) * mm});
            skLineSegment(sketch, "E297", {"start": v(-15.65, 12.25) * mm, "end": v(-16.02, 12.3) * mm});
            skLineSegment(sketch, "E298", {"start": v(-16.02, 12.3) * mm, "end": v(-16.44, 12.3) * mm});
            skLineSegment(sketch, "E299", {"start": v(-16.44, 12.3) * mm, "end": v(-16.9, 12.25) * mm});
            skLineSegment(sketch, "E300", {"start": v(-16.9, 12.25) * mm, "end": v(-17.39, 12.14) * mm});
            skArc(sketch, "E301", {"start": v(-17.39, 12.14) * mm, "mid": v(-17.55, 11.77) * mm, "end": v(-17.7, 11.4) * mm});
            skLineSegment(sketch, "E302", {"start": v(-15.24, 9.75) * mm, "end": v(-15.66, 9.83) * mm});
            skLineSegment(sketch, "E303", {"start": v(-15.66, 9.83) * mm, "end": v(-15.98, 9.89) * mm});
            skLineSegment(sketch, "E304", {"start": v(-15.98, 9.89) * mm, "end": v(-16.14, 9.92) * mm});
            skLineSegment(sketch, "E305", {"start": v(-16.14, 9.92) * mm, "end": v(-16.2, 9.93) * mm});
            skLineSegment(sketch, "E306", {"start": v(-16.2, 9.93) * mm, "end": v(-16.23, 9.94) * mm});
            skLineSegment(sketch, "E307", {"start": v(-16.23, 9.94) * mm, "end": v(-16.28, 9.96) * mm});
            skLineSegment(sketch, "E308", {"start": v(-16.28, 9.96) * mm, "end": v(-16.54, 10.1) * mm});
            skLineSegment(sketch, "E309", {"start": v(-16.54, 10.1) * mm, "end": v(-16.84, 10.32) * mm});
            skLineSegment(sketch, "E310", {"start": v(-16.84, 10.32) * mm, "end": v(-17.14, 10.61) * mm});
            skLineSegment(sketch, "E311", {"start": v(-17.14, 10.61) * mm, "end": v(-17.43, 10.97) * mm});
            skLineSegment(sketch, "E312", {"start": v(-17.43, 10.97) * mm, "end": v(-17.7, 11.4) * mm});
            skArc(sketch, "E313", {"start": v(-14.74, 9.12) * mm, "mid": v(-14.87, 9.53) * mm, "end": v(-15.24, 9.75) * mm});
            skArc(sketch, "E314", {"start": v(-14.74, 9.12) * mm, "mid": v(-14.75, 8.9) * mm, "end": v(-14.74, 8.69) * mm});
            skArc(sketch, "E315", {"start": v(-15.24, 8.06) * mm, "mid": v(-14.87, 8.28) * mm, "end": v(-14.74, 8.69) * mm});
            skLineSegment(sketch, "E316", {"start": v(-15.24, 8.06) * mm, "end": v(-15.66, 7.98) * mm});
            skLineSegment(sketch, "E317", {"start": v(-15.66, 7.98) * mm, "end": v(-15.98, 7.92) * mm});
            skLineSegment(sketch, "E318", {"start": v(-15.98, 7.92) * mm, "end": v(-16.14, 7.9) * mm});
            skLineSegment(sketch, "E319", {"start": v(-16.14, 7.9) * mm, "end": v(-16.2, 7.88) * mm});
            skLineSegment(sketch, "E320", {"start": v(-16.2, 7.88) * mm, "end": v(-16.23, 7.87) * mm});
            skLineSegment(sketch, "E321", {"start": v(-16.23, 7.87) * mm, "end": v(-16.28, 7.85) * mm});
            skLineSegment(sketch, "E322", {"start": v(-16.28, 7.85) * mm, "end": v(-16.54, 7.71) * mm});
            skLineSegment(sketch, "E323", {"start": v(-16.54, 7.71) * mm, "end": v(-16.84, 7.5) * mm});
            skLineSegment(sketch, "E324", {"start": v(-16.84, 7.5) * mm, "end": v(-17.14, 7.2) * mm});
            skLineSegment(sketch, "E325", {"start": v(-17.14, 7.2) * mm, "end": v(-17.43, 6.83) * mm});
            skLineSegment(sketch, "E326", {"start": v(-17.43, 6.83) * mm, "end": v(-17.7, 6.41) * mm});
            skArc(sketch, "E327", {"start": v(-17.7, 6.41) * mm, "mid": v(-17.55, 6.03) * mm, "end": v(-17.39, 5.66) * mm});
            skLineSegment(sketch, "E328", {"start": v(-14.49, 6.24) * mm, "end": v(-14.84, 6) * mm});
            skLineSegment(sketch, "E329", {"start": v(-14.84, 6) * mm, "end": v(-15.1, 5.8) * mm});
            skLineSegment(sketch, "E330", {"start": v(-15.1, 5.8) * mm, "end": v(-15.24, 5.72) * mm});
            skLineSegment(sketch, "E331", {"start": v(-15.24, 5.72) * mm, "end": v(-15.29, 5.69) * mm});
            skLineSegment(sketch, "E332", {"start": v(-15.29, 5.69) * mm, "end": v(-15.32, 5.67) * mm});
            skLineSegment(sketch, "E333", {"start": v(-15.32, 5.67) * mm, "end": v(-15.37, 5.65) * mm});
            skLineSegment(sketch, "E334", {"start": v(-15.37, 5.65) * mm, "end": v(-15.65, 5.56) * mm});
            skLineSegment(sketch, "E335", {"start": v(-15.65, 5.56) * mm, "end": v(-16.02, 5.5) * mm});
            skLineSegment(sketch, "E336", {"start": v(-16.02, 5.5) * mm, "end": v(-16.44, 5.5) * mm});
            skLineSegment(sketch, "E337", {"start": v(-16.44, 5.5) * mm, "end": v(-16.9, 5.55) * mm});
            skLineSegment(sketch, "E338", {"start": v(-16.9, 5.55) * mm, "end": v(-17.39, 5.66) * mm});
            skArc(sketch, "E339", {"start": v(-13.7, 6.15) * mm, "mid": v(-14.07, 6.34) * mm, "end": v(-14.49, 6.24) * mm});
            skArc(sketch, "E340", {"start": v(-13.7, 6.15) * mm, "mid": v(-13.54, 5.99) * mm, "end": v(-13.38, 5.84) * mm});
            skArc(sketch, "E341", {"start": v(-13.29, 5.04) * mm, "mid": v(-13.19, 5.46) * mm, "end": v(-13.38, 5.84) * mm});
            skLineSegment(sketch, "E342", {"start": v(-13.29, 5.04) * mm, "end": v(-13.53, 4.7) * mm});
            skLineSegment(sketch, "E343", {"start": v(-13.53, 4.7) * mm, "end": v(-13.72, 4.42) * mm});
            skLineSegment(sketch, "E344", {"start": v(-13.72, 4.42) * mm, "end": v(-13.8, 4.29) * mm});
            skLineSegment(sketch, "E345", {"start": v(-13.8, 4.29) * mm, "end": v(-13.84, 4.24) * mm});
            skLineSegment(sketch, "E346", {"start": v(-13.84, 4.24) * mm, "end": v(-13.86, 4.2) * mm});
            skLineSegment(sketch, "E347", {"start": v(-13.86, 4.2) * mm, "end": v(-13.88, 4.16) * mm});
            skLineSegment(sketch, "E348", {"start": v(-13.88, 4.16) * mm, "end": v(-13.97, 3.88) * mm});
            skLineSegment(sketch, "E349", {"start": v(-13.97, 3.88) * mm, "end": v(-14.02, 3.5) * mm});
            skLineSegment(sketch, "E350", {"start": v(-14.02, 3.5) * mm, "end": v(-14.03, 3.09) * mm});
            skLineSegment(sketch, "E351", {"start": v(-14.03, 3.09) * mm, "end": v(-13.97, 2.63) * mm});
            skLineSegment(sketch, "E352", {"start": v(-13.97, 2.63) * mm, "end": v(-13.86, 2.14) * mm});
            skArc(sketch, "E353", {"start": v(-13.86, 2.14) * mm, "mid": v(-13.5, 1.97) * mm, "end": v(-13.12, 1.83) * mm});
            skLineSegment(sketch, "E354", {"start": v(-11.47, 4.29) * mm, "end": v(-11.55, 3.87) * mm});
            skLineSegment(sketch, "E355", {"start": v(-11.55, 3.87) * mm, "end": v(-11.6, 3.55) * mm});
            skLineSegment(sketch, "E356", {"start": v(-11.6, 3.55) * mm, "end": v(-11.64, 3.39) * mm});
            skLineSegment(sketch, "E357", {"start": v(-11.64, 3.39) * mm, "end": v(-11.65, 3.33) * mm});
            skLineSegment(sketch, "E358", {"start": v(-11.65, 3.33) * mm, "end": v(-11.66, 3.3) * mm});
            skLineSegment(sketch, "E359", {"start": v(-11.66, 3.3) * mm, "end": v(-11.68, 3.25) * mm});
            skLineSegment(sketch, "E360", {"start": v(-11.68, 3.25) * mm, "end": v(-11.82, 2.98) * mm});
            skLineSegment(sketch, "E361", {"start": v(-11.82, 2.98) * mm, "end": v(-12.04, 2.69) * mm});
            skLineSegment(sketch, "E362", {"start": v(-12.04, 2.69) * mm, "end": v(-12.33, 2.39) * mm});
            skLineSegment(sketch, "E363", {"start": v(-12.33, 2.39) * mm, "end": v(-12.7, 2.1) * mm});
            skLineSegment(sketch, "E364", {"start": v(-12.7, 2.1) * mm, "end": v(-13.12, 1.83) * mm});
            skArc(sketch, "E365", {"start": v(-10.84, 4.78) * mm, "mid": v(-11.25, 4.66) * mm, "end": v(-11.47, 4.29) * mm});
            skArc(sketch, "E366", {"start": v(-10.84, 4.78) * mm, "mid": v(-10.62, 4.78) * mm, "end": v(-10.4, 4.78) * mm});
            skArc(sketch, "E367", {"start": v(-9.78, 4.29) * mm, "mid": v(-10, 4.66) * mm, "end": v(-10.4, 4.78) * mm});
            skLineSegment(sketch, "E368", {"start": v(-9.78, 4.29) * mm, "end": v(-9.7, 3.87) * mm});
            skLineSegment(sketch, "E369", {"start": v(-9.7, 3.87) * mm, "end": v(-9.64, 3.55) * mm});
            skLineSegment(sketch, "E370", {"start": v(-9.64, 3.55) * mm, "end": v(-9.61, 3.39) * mm});
            skLineSegment(sketch, "E371", {"start": v(-9.61, 3.39) * mm, "end": v(-9.6, 3.33) * mm});
            skLineSegment(sketch, "E372", {"start": v(-9.6, 3.33) * mm, "end": v(-9.59, 3.3) * mm});
            skLineSegment(sketch, "E373", {"start": v(-9.59, 3.3) * mm, "end": v(-9.57, 3.25) * mm});
            skLineSegment(sketch, "E374", {"start": v(-9.57, 3.25) * mm, "end": v(-9.43, 2.98) * mm});
            skLineSegment(sketch, "E375", {"start": v(-9.43, 2.98) * mm, "end": v(-9.21, 2.69) * mm});
            skLineSegment(sketch, "E376", {"start": v(-9.21, 2.69) * mm, "end": v(-8.92, 2.39) * mm});
            skLineSegment(sketch, "E377", {"start": v(-8.92, 2.39) * mm, "end": v(-8.55, 2.1) * mm});
            skLineSegment(sketch, "E378", {"start": v(-8.55, 2.1) * mm, "end": v(-8.13, 1.83) * mm});
            skArc(sketch, "E379", {"start": v(-8.13, 1.83) * mm, "mid": v(-7.75, 1.97) * mm, "end": v(-7.38, 2.14) * mm});
            skLineSegment(sketch, "E380", {"start": v(-7.96, 5.04) * mm, "end": v(-7.72, 4.7) * mm});
            skLineSegment(sketch, "E381", {"start": v(-7.72, 4.7) * mm, "end": v(-7.53, 4.42) * mm});
            skLineSegment(sketch, "E382", {"start": v(-7.53, 4.42) * mm, "end": v(-7.44, 4.29) * mm});
            skLineSegment(sketch, "E383", {"start": v(-7.44, 4.29) * mm, "end": v(-7.4, 4.24) * mm});
            skLineSegment(sketch, "E384", {"start": v(-7.4, 4.24) * mm, "end": v(-7.4, 4.2) * mm});
            skLineSegment(sketch, "E385", {"start": v(-7.4, 4.2) * mm, "end": v(-7.37, 4.16) * mm});
            skLineSegment(sketch, "E386", {"start": v(-7.37, 4.16) * mm, "end": v(-7.28, 3.88) * mm});
            skLineSegment(sketch, "E387", {"start": v(-7.28, 3.88) * mm, "end": v(-7.23, 3.5) * mm});
            skLineSegment(sketch, "E388", {"start": v(-7.23, 3.5) * mm, "end": v(-7.22, 3.09) * mm});
            skLineSegment(sketch, "E389", {"start": v(-7.22, 3.09) * mm, "end": v(-7.27, 2.63) * mm});
            skLineSegment(sketch, "E390", {"start": v(-7.27, 2.63) * mm, "end": v(-7.38, 2.14) * mm});
            skArc(sketch, "E391", {"start": v(-7.87, 5.84) * mm, "mid": v(-8.06, 5.46) * mm, "end": v(-7.96, 5.04) * mm});
            skArc(sketch, "E392", {"start": v(-7.87, 5.84) * mm, "mid": v(-7.7, 5.99) * mm, "end": v(-7.56, 6.15) * mm});
            skArc(sketch, "E393", {"start": v(12.61, 13.68) * mm, "mid": v(12.68, 13.33) * mm, "end": v(12.97, 13.12) * mm});
            skLineSegment(sketch, "E394", {"start": v(12.61, 13.68) * mm, "end": v(12.66, 13.97) * mm});
            skLineSegment(sketch, "E395", {"start": v(12.66, 13.97) * mm, "end": v(12.7, 14.2) * mm});
            skLineSegment(sketch, "E396", {"start": v(12.7, 14.2) * mm, "end": v(12.72, 14.3) * mm});
            skLineSegment(sketch, "E397", {"start": v(12.72, 14.3) * mm, "end": v(12.73, 14.36) * mm});
            skLineSegment(sketch, "E398", {"start": v(12.73, 14.36) * mm, "end": v(12.73, 14.43) * mm});
            skLineSegment(sketch, "E399", {"start": v(12.73, 14.43) * mm, "end": v(12.71, 14.65) * mm});
            skLineSegment(sketch, "E400", {"start": v(12.71, 14.65) * mm, "end": v(12.65, 14.93) * mm});
            skLineSegment(sketch, "E401", {"start": v(12.65, 14.93) * mm, "end": v(12.54, 15.23) * mm});
            skLineSegment(sketch, "E402", {"start": v(12.54, 15.23) * mm, "end": v(12.36, 15.6) * mm});
            skLineSegment(sketch, "E403", {"start": v(12.36, 15.6) * mm, "end": v(12.11, 15.98) * mm});
            skArc(sketch, "E404", {"start": v(12.11, 15.98) * mm, "mid": v(11.76, 15.99) * mm, "end": v(11.4, 15.98) * mm});
            skLineSegment(sketch, "E405", {"start": v(10.91, 13.68) * mm, "end": v(10.86, 13.97) * mm});
            skLineSegment(sketch, "E406", {"start": v(10.86, 13.97) * mm, "end": v(10.82, 14.2) * mm});
            skLineSegment(sketch, "E407", {"start": v(10.82, 14.2) * mm, "end": v(10.8, 14.3) * mm});
            skLineSegment(sketch, "E408", {"start": v(10.8, 14.3) * mm, "end": v(10.8, 14.36) * mm});
            skLineSegment(sketch, "E409", {"start": v(10.8, 14.36) * mm, "end": v(10.8, 14.43) * mm});
            skLineSegment(sketch, "E410", {"start": v(10.8, 14.43) * mm, "end": v(10.81, 14.65) * mm});
            skLineSegment(sketch, "E411", {"start": v(10.81, 14.65) * mm, "end": v(10.88, 14.93) * mm});
            skLineSegment(sketch, "E412", {"start": v(10.88, 14.93) * mm, "end": v(10.98, 15.23) * mm});
            skLineSegment(sketch, "E413", {"start": v(10.98, 15.23) * mm, "end": v(11.17, 15.6) * mm});
            skLineSegment(sketch, "E414", {"start": v(10.82, 3.38) * mm, "end": v(10.8, 3.27) * mm});
            skLineSegment(sketch, "E415", {"start": v(10.8, 3.27) * mm, "end": v(10.8, 3.21) * mm});
            skLineSegment(sketch, "E416", {"start": v(10.8, 3.21) * mm, "end": v(10.8, 3.14) * mm});
            skLineSegment(sketch, "E417", {"start": v(10.8, 3.14) * mm, "end": v(10.81, 2.92) * mm});
            skLineSegment(sketch, "E418", {"start": v(10.81, 2.92) * mm, "end": v(10.88, 2.65) * mm});
            skLineSegment(sketch, "E419", {"start": v(10.88, 2.65) * mm, "end": v(10.98, 2.35) * mm});
            skLineSegment(sketch, "E420", {"start": v(10.98, 2.35) * mm, "end": v(11.17, 1.97) * mm});
            skLineSegment(sketch, "E421", {"start": v(11.17, 1.97) * mm, "end": v(11.4, 1.6) * mm});
            skArc(sketch, "E422", {"start": v(11.4, 1.6) * mm, "mid": v(11.76, 1.59) * mm, "end": v(12.11, 1.6) * mm});
            skLineSegment(sketch, "E423", {"start": v(12.61, 3.89) * mm, "end": v(12.66, 3.6) * mm});
            skLineSegment(sketch, "E424", {"start": v(12.66, 3.6) * mm, "end": v(12.7, 3.38) * mm});
            skLineSegment(sketch, "E425", {"start": v(12.7, 3.38) * mm, "end": v(12.72, 3.27) * mm});
            skLineSegment(sketch, "E426", {"start": v(12.72, 3.27) * mm, "end": v(12.73, 3.21) * mm});
            skLineSegment(sketch, "E427", {"start": v(12.73, 3.21) * mm, "end": v(12.73, 3.14) * mm});
            skLineSegment(sketch, "E428", {"start": v(12.73, 3.14) * mm, "end": v(12.71, 2.92) * mm});
            skLineSegment(sketch, "E429", {"start": v(12.71, 2.92) * mm, "end": v(12.65, 2.65) * mm});
            skLineSegment(sketch, "E430", {"start": v(12.65, 2.65) * mm, "end": v(12.54, 2.35) * mm});
            skLineSegment(sketch, "E431", {"start": v(12.54, 2.35) * mm, "end": v(12.36, 1.97) * mm});
            skLineSegment(sketch, "E432", {"start": v(12.36, 1.97) * mm, "end": v(12.11, 1.6) * mm});
            skArc(sketch, "E433", {"start": v(12.97, 4.45) * mm, "mid": v(12.68, 4.24) * mm, "end": v(12.61, 3.89) * mm});
            skCircle(sketch, "E434", {"center": v(-14.23, -33.23) * mm, "radius": 11 * mm});
            skArc(sketch, "E435", {"start": v(12.97, 4.45) * mm, "mid": v(13.15, 4.5) * mm, "end": v(13.33, 4.57) * mm});
            skArc(sketch, "E436", {"start": v(13.95, 4.32) * mm, "mid": v(13.7, 4.57) * mm, "end": v(13.33, 4.57) * mm});
            skLineSegment(sketch, "E437", {"start": v(13.95, 4.32) * mm, "end": v(14.08, 4.06) * mm});
            skLineSegment(sketch, "E438", {"start": v(14.08, 4.06) * mm, "end": v(14.18, 3.86) * mm});
            skLineSegment(sketch, "E439", {"start": v(14.18, 3.86) * mm, "end": v(14.23, 3.76) * mm});
            skLineSegment(sketch, "E440", {"start": v(14.23, 3.76) * mm, "end": v(14.26, 3.7) * mm});
            skLineSegment(sketch, "E441", {"start": v(14.26, 3.7) * mm, "end": v(14.3, 3.65) * mm});
            skLineSegment(sketch, "E442", {"start": v(14.3, 3.65) * mm, "end": v(14.44, 3.48) * mm});
            skLineSegment(sketch, "E443", {"start": v(14.44, 3.48) * mm, "end": v(14.65, 3.3) * mm});
            skLineSegment(sketch, "E444", {"start": v(14.65, 3.3) * mm, "end": v(14.92, 3.12) * mm});
            skLineSegment(sketch, "E445", {"start": v(14.92, 3.12) * mm, "end": v(15.28, 2.93) * mm});
            skLineSegment(sketch, "E446", {"start": v(15.28, 2.93) * mm, "end": v(15.7, 2.76) * mm});
            skArc(sketch, "E447", {"start": v(15.7, 2.76) * mm, "mid": v(16, 2.96) * mm, "end": v(16.27, 3.18) * mm});
            skLineSegment(sketch, "E448", {"start": v(15.33, 5.33) * mm, "end": v(15.54, 5.12) * mm});
            skLineSegment(sketch, "E449", {"start": v(15.54, 5.12) * mm, "end": v(15.7, 4.97) * mm});
            skLineSegment(sketch, "E450", {"start": v(15.7, 4.97) * mm, "end": v(15.78, 4.88) * mm});
            skLineSegment(sketch, "E451", {"start": v(15.78, 4.88) * mm, "end": v(15.82, 4.85) * mm});
            skLineSegment(sketch, "E452", {"start": v(15.82, 4.85) * mm, "end": v(15.86, 4.8) * mm});
            skLineSegment(sketch, "E453", {"start": v(15.86, 4.8) * mm, "end": v(15.98, 4.6) * mm});
            skLineSegment(sketch, "E454", {"start": v(15.98, 4.6) * mm, "end": v(16.09, 4.34) * mm});
            skLineSegment(sketch, "E455", {"start": v(16.09, 4.34) * mm, "end": v(16.18, 4.04) * mm});
            skLineSegment(sketch, "E456", {"start": v(16.18, 4.04) * mm, "end": v(16.25, 3.63) * mm});
            skLineSegment(sketch, "E457", {"start": v(16.25, 3.63) * mm, "end": v(16.27, 3.18) * mm});
            skArc(sketch, "E458", {"start": v(15.29, 5.99) * mm, "mid": v(15.18, 5.65) * mm, "end": v(15.33, 5.33) * mm});
            skArc(sketch, "E459", {"start": v(15.29, 5.99) * mm, "mid": v(15.4, 6.14) * mm, "end": v(15.51, 6.3) * mm});
            skArc(sketch, "E460", {"start": v(16.16, 6.46) * mm, "mid": v(15.8, 6.5) * mm, "end": v(15.51, 6.3) * mm});
            skLineSegment(sketch, "E461", {"start": v(16.16, 6.46) * mm, "end": v(16.41, 6.33) * mm});
            skLineSegment(sketch, "E462", {"start": v(16.41, 6.33) * mm, "end": v(16.61, 6.22) * mm});
            skLineSegment(sketch, "E463", {"start": v(16.61, 6.22) * mm, "end": v(16.72, 6.17) * mm});
            skLineSegment(sketch, "E464", {"start": v(16.72, 6.17) * mm, "end": v(16.76, 6.14) * mm});
            skLineSegment(sketch, "E465", {"start": v(17.36, 9.59) * mm, "end": v(17.43, 9.6) * mm});
            skLineSegment(sketch, "E466", {"start": v(17.43, 9.6) * mm, "end": v(17.63, 9.7) * mm});
            skLineSegment(sketch, "E467", {"start": v(17.63, 9.7) * mm, "end": v(17.87, 9.84) * mm});
            skLineSegment(sketch, "E468", {"start": v(17.87, 9.84) * mm, "end": v(18.13, 10.04) * mm});
            skLineSegment(sketch, "E469", {"start": v(18.13, 10.04) * mm, "end": v(18.42, 10.33) * mm});
            skLineSegment(sketch, "E470", {"start": v(18.42, 10.33) * mm, "end": v(18.71, 10.67) * mm});
            skArc(sketch, "E471", {"start": v(18.71, 10.67) * mm, "mid": v(18.6, 11.01) * mm, "end": v(18.5, 11.34) * mm});
            skLineSegment(sketch, "E472", {"start": v(16.16, 11.1) * mm, "end": v(16.41, 11.25) * mm});
            skLineSegment(sketch, "E473", {"start": v(16.41, 11.25) * mm, "end": v(16.61, 11.35) * mm});
            skLineSegment(sketch, "E474", {"start": v(16.61, 11.35) * mm, "end": v(16.72, 11.4) * mm});
            skLineSegment(sketch, "E475", {"start": v(16.72, 11.4) * mm, "end": v(16.76, 11.43) * mm});
            skLineSegment(sketch, "E476", {"start": v(16.76, 11.43) * mm, "end": v(16.83, 11.45) * mm});
            skArc(sketch, "E477", {"start": v(15.51, 11.27) * mm, "mid": v(15.4, 11.43) * mm, "end": v(15.29, 11.59) * mm});
            skArc(sketch, "E478", {"start": v(15.33, 12.25) * mm, "mid": v(15.18, 11.92) * mm, "end": v(15.29, 11.59) * mm});
            skLineSegment(sketch, "E479", {"start": v(15.33, 12.25) * mm, "end": v(15.54, 12.45) * mm});
            skLineSegment(sketch, "E480", {"start": v(15.54, 12.45) * mm, "end": v(15.7, 12.6) * mm});
            skArc(sketch, "E481", {"start": v(15.51, 11.27) * mm, "mid": v(15.8, 11.07) * mm, "end": v(16.16, 11.1) * mm});
            skLineSegment(sketch, "E482", {"start": v(18.06, 11.46) * mm, "end": v(18.5, 11.34) * mm});
            skLineSegment(sketch, "E483", {"start": v(17.65, 11.52) * mm, "end": v(18.06, 11.46) * mm});
            skLineSegment(sketch, "E484", {"start": v(17.33, 11.53) * mm, "end": v(17.65, 11.52) * mm});
            skLineSegment(sketch, "E485", {"start": v(17.05, 11.5) * mm, "end": v(17.33, 11.53) * mm});
            skLineSegment(sketch, "E486", {"start": v(16.83, 11.45) * mm, "end": v(17.05, 11.5) * mm});
            skLineSegment(sketch, "E487", {"start": v(17.3, 9.58) * mm, "end": v(17.36, 9.59) * mm});
            skLineSegment(sketch, "E488", {"start": v(17.2, 9.56) * mm, "end": v(17.3, 9.58) * mm});
            skLineSegment(sketch, "E489", {"start": v(16.97, 9.53) * mm, "end": v(17.2, 9.56) * mm});
            skLineSegment(sketch, "E490", {"start": v(16.68, 9.49) * mm, "end": v(16.97, 9.53) * mm});
            skArc(sketch, "E491", {"start": v(16.68, 9.49) * mm, "mid": v(16.37, 9.32) * mm, "end": v(16.26, 8.98) * mm});
            skArc(sketch, "E492", {"start": v(16.26, 8.6) * mm, "mid": v(16.26, 8.79) * mm, "end": v(16.26, 8.98) * mm});
            skArc(sketch, "E493", {"start": v(16.26, 8.6) * mm, "mid": v(16.37, 8.26) * mm, "end": v(16.68, 8.08) * mm});
            skLineSegment(sketch, "E494", {"start": v(18.42, 7.25) * mm, "end": v(18.71, 6.9) * mm});
            skLineSegment(sketch, "E495", {"start": v(18.13, 7.54) * mm, "end": v(18.42, 7.25) * mm});
            skLineSegment(sketch, "E496", {"start": v(17.87, 7.73) * mm, "end": v(18.13, 7.54) * mm});
            skLineSegment(sketch, "E497", {"start": v(17.63, 7.88) * mm, "end": v(17.87, 7.73) * mm});
            skLineSegment(sketch, "E498", {"start": v(17.43, 7.97) * mm, "end": v(17.63, 7.88) * mm});
            skLineSegment(sketch, "E499", {"start": v(17.36, 7.98) * mm, "end": v(17.43, 7.97) * mm});
            skLineSegment(sketch, "E500", {"start": v(17.3, 8) * mm, "end": v(17.36, 7.98) * mm});
            skLineSegment(sketch, "E501", {"start": v(17.2, 8.01) * mm, "end": v(17.3, 8) * mm});
            skLineSegment(sketch, "E502", {"start": v(16.97, 8.04) * mm, "end": v(17.2, 8.01) * mm});
            skLineSegment(sketch, "E503", {"start": v(16.68, 8.08) * mm, "end": v(16.97, 8.04) * mm});
            skArc(sketch, "E504", {"start": v(18.5, 6.23) * mm, "mid": v(18.6, 6.56) * mm, "end": v(18.71, 6.9) * mm});
            skLineSegment(sketch, "E505", {"start": v(18.06, 6.12) * mm, "end": v(18.5, 6.23) * mm});
            skLineSegment(sketch, "E506", {"start": v(17.65, 6.06) * mm, "end": v(18.06, 6.12) * mm});
            skLineSegment(sketch, "E507", {"start": v(17.33, 6.05) * mm, "end": v(17.65, 6.06) * mm});
            skLineSegment(sketch, "E508", {"start": v(17.05, 6.07) * mm, "end": v(17.33, 6.05) * mm});
            skLineSegment(sketch, "E509", {"start": v(16.83, 6.12) * mm, "end": v(17.05, 6.07) * mm});
            skLineSegment(sketch, "E510", {"start": v(16.76, 6.14) * mm, "end": v(16.83, 6.12) * mm});
            skLineSegment(sketch, "E511", {"start": v(10.86, 3.6) * mm, "end": v(10.82, 3.38) * mm});
            skLineSegment(sketch, "E512", {"start": v(10.91, 3.89) * mm, "end": v(10.86, 3.6) * mm});
            skArc(sketch, "E513", {"start": v(10.91, 3.89) * mm, "mid": v(10.84, 4.24) * mm, "end": v(10.56, 4.45) * mm});
            skArc(sketch, "E514", {"start": v(10.19, 4.57) * mm, "mid": v(10.37, 4.5) * mm, "end": v(10.56, 4.45) * mm});
            skArc(sketch, "E515", {"start": v(10.19, 4.57) * mm, "mid": v(9.83, 4.57) * mm, "end": v(9.57, 4.32) * mm});
            skLineSegment(sketch, "E516", {"start": v(8.24, 2.93) * mm, "end": v(7.82, 2.76) * mm});
            skLineSegment(sketch, "E517", {"start": v(8.6, 3.12) * mm, "end": v(8.24, 2.93) * mm});
            skLineSegment(sketch, "E518", {"start": v(8.87, 3.3) * mm, "end": v(8.6, 3.12) * mm});
            skLineSegment(sketch, "E519", {"start": v(9.08, 3.48) * mm, "end": v(8.87, 3.3) * mm});
            skLineSegment(sketch, "E520", {"start": v(9.23, 3.65) * mm, "end": v(9.08, 3.48) * mm});
            skLineSegment(sketch, "E521", {"start": v(9.27, 3.7) * mm, "end": v(9.23, 3.65) * mm});
            skLineSegment(sketch, "E522", {"start": v(9.3, 3.76) * mm, "end": v(9.27, 3.7) * mm});
            skLineSegment(sketch, "E523", {"start": v(9.35, 3.86) * mm, "end": v(9.3, 3.76) * mm});
            skLineSegment(sketch, "E524", {"start": v(9.45, 4.06) * mm, "end": v(9.35, 3.86) * mm});
            skLineSegment(sketch, "E525", {"start": v(9.57, 4.32) * mm, "end": v(9.45, 4.06) * mm});
            skArc(sketch, "E526", {"start": v(7.25, 3.18) * mm, "mid": v(7.53, 2.96) * mm, "end": v(7.82, 2.76) * mm});
            skLineSegment(sketch, "E527", {"start": v(7.28, 3.63) * mm, "end": v(7.25, 3.18) * mm});
            skLineSegment(sketch, "E528", {"start": v(7.35, 4.04) * mm, "end": v(7.28, 3.63) * mm});
            skLineSegment(sketch, "E529", {"start": v(7.44, 4.34) * mm, "end": v(7.35, 4.04) * mm});
            skLineSegment(sketch, "E530", {"start": v(7.55, 4.6) * mm, "end": v(7.44, 4.34) * mm});
            skLineSegment(sketch, "E531", {"start": v(7.66, 4.8) * mm, "end": v(7.55, 4.6) * mm});
            skLineSegment(sketch, "E532", {"start": v(7.7, 4.85) * mm, "end": v(7.66, 4.8) * mm});
            skLineSegment(sketch, "E533", {"start": v(7.74, 4.88) * mm, "end": v(7.7, 4.85) * mm});
            skLineSegment(sketch, "E534", {"start": v(7.82, 4.97) * mm, "end": v(7.74, 4.88) * mm});
            skLineSegment(sketch, "E535", {"start": v(7.99, 5.12) * mm, "end": v(7.82, 4.97) * mm});
            skLineSegment(sketch, "E536", {"start": v(8.2, 5.33) * mm, "end": v(7.99, 5.12) * mm});
            skArc(sketch, "E537", {"start": v(8.2, 5.33) * mm, "mid": v(8.34, 5.65) * mm, "end": v(8.24, 5.99) * mm});
            skArc(sketch, "E538", {"start": v(8.01, 6.3) * mm, "mid": v(8.12, 6.14) * mm, "end": v(8.24, 5.99) * mm});
            skArc(sketch, "E539", {"start": v(8.01, 6.3) * mm, "mid": v(7.72, 6.5) * mm, "end": v(7.37, 6.46) * mm});
            skLineSegment(sketch, "E540", {"start": v(5.47, 6.12) * mm, "end": v(5.03, 6.23) * mm});
            skLineSegment(sketch, "E541", {"start": v(5.88, 6.06) * mm, "end": v(5.47, 6.12) * mm});
            skLineSegment(sketch, "E542", {"start": v(6.2, 6.05) * mm, "end": v(5.88, 6.06) * mm});
            skLineSegment(sketch, "E543", {"start": v(6.48, 6.07) * mm, "end": v(6.2, 6.05) * mm});
            skLineSegment(sketch, "E544", {"start": v(6.7, 6.12) * mm, "end": v(6.48, 6.07) * mm});
            skLineSegment(sketch, "E545", {"start": v(6.76, 6.14) * mm, "end": v(6.7, 6.12) * mm});
            skLineSegment(sketch, "E546", {"start": v(6.8, 6.17) * mm, "end": v(6.76, 6.14) * mm});
            skLineSegment(sketch, "E547", {"start": v(6.91, 6.22) * mm, "end": v(6.8, 6.17) * mm});
            skLineSegment(sketch, "E548", {"start": v(7.11, 6.33) * mm, "end": v(6.91, 6.22) * mm});
            skLineSegment(sketch, "E549", {"start": v(7.37, 6.46) * mm, "end": v(7.11, 6.33) * mm});
            skArc(sketch, "E550", {"start": v(4.81, 6.9) * mm, "mid": v(4.91, 6.56) * mm, "end": v(5.03, 6.23) * mm});
            skLineSegment(sketch, "E551", {"start": v(5.1, 7.25) * mm, "end": v(4.81, 6.9) * mm});
            skLineSegment(sketch, "E552", {"start": v(5.4, 7.54) * mm, "end": v(5.1, 7.25) * mm});
            skLineSegment(sketch, "E553", {"start": v(5.65, 7.73) * mm, "end": v(5.4, 7.54) * mm});
            skLineSegment(sketch, "E554", {"start": v(5.89, 7.88) * mm, "end": v(5.65, 7.73) * mm});
            skLineSegment(sketch, "E555", {"start": v(6.1, 7.97) * mm, "end": v(5.89, 7.88) * mm});
            skLineSegment(sketch, "E556", {"start": v(6.16, 7.98) * mm, "end": v(6.1, 7.97) * mm});
            skLineSegment(sketch, "E557", {"start": v(6.21, 8) * mm, "end": v(6.16, 7.98) * mm});
            skLineSegment(sketch, "E558", {"start": v(6.33, 8.01) * mm, "end": v(6.21, 8) * mm});
            skLineSegment(sketch, "E559", {"start": v(6.56, 8.04) * mm, "end": v(6.33, 8.01) * mm});
            skLineSegment(sketch, "E560", {"start": v(6.84, 8.08) * mm, "end": v(6.56, 8.04) * mm});
            skArc(sketch, "E561", {"start": v(6.84, 8.08) * mm, "mid": v(7.15, 8.26) * mm, "end": v(7.27, 8.6) * mm});
            skArc(sketch, "E562", {"start": v(7.27, 8.98) * mm, "mid": v(7.26, 8.79) * mm, "end": v(7.27, 8.6) * mm});
            skArc(sketch, "E563", {"start": v(7.27, 8.98) * mm, "mid": v(7.15, 9.32) * mm, "end": v(6.84, 9.49) * mm});
            skLineSegment(sketch, "E564", {"start": v(5.1, 10.33) * mm, "end": v(4.81, 10.67) * mm});
            skLineSegment(sketch, "E565", {"start": v(5.4, 10.04) * mm, "end": v(5.1, 10.33) * mm});
            skLineSegment(sketch, "E566", {"start": v(5.65, 9.84) * mm, "end": v(5.4, 10.04) * mm});
            skLineSegment(sketch, "E567", {"start": v(5.89, 9.7) * mm, "end": v(5.65, 9.84) * mm});
            skLineSegment(sketch, "E568", {"start": v(6.1, 9.6) * mm, "end": v(5.89, 9.7) * mm});
            skLineSegment(sketch, "E569", {"start": v(6.16, 9.59) * mm, "end": v(6.1, 9.6) * mm});
            skLineSegment(sketch, "E570", {"start": v(6.21, 9.58) * mm, "end": v(6.16, 9.59) * mm});
            skLineSegment(sketch, "E571", {"start": v(6.33, 9.56) * mm, "end": v(6.21, 9.58) * mm});
            skLineSegment(sketch, "E572", {"start": v(6.56, 9.53) * mm, "end": v(6.33, 9.56) * mm});
            skLineSegment(sketch, "E573", {"start": v(6.84, 9.49) * mm, "end": v(6.56, 9.53) * mm});
            skArc(sketch, "E574", {"start": v(5.03, 11.34) * mm, "mid": v(4.91, 11.01) * mm, "end": v(4.81, 10.67) * mm});
            skLineSegment(sketch, "E575", {"start": v(5.47, 11.46) * mm, "end": v(5.03, 11.34) * mm});
            skLineSegment(sketch, "E576", {"start": v(5.88, 11.52) * mm, "end": v(5.47, 11.46) * mm});
            skLineSegment(sketch, "E577", {"start": v(6.2, 11.53) * mm, "end": v(5.88, 11.52) * mm});
            skLineSegment(sketch, "E578", {"start": v(6.48, 11.5) * mm, "end": v(6.2, 11.53) * mm});
            skLineSegment(sketch, "E579", {"start": v(6.7, 11.45) * mm, "end": v(6.48, 11.5) * mm});
            skLineSegment(sketch, "E580", {"start": v(6.76, 11.43) * mm, "end": v(6.7, 11.45) * mm});
            skLineSegment(sketch, "E581", {"start": v(6.8, 11.4) * mm, "end": v(6.76, 11.43) * mm});
            skLineSegment(sketch, "E582", {"start": v(6.91, 11.35) * mm, "end": v(6.8, 11.4) * mm});
            skLineSegment(sketch, "E583", {"start": v(7.11, 11.25) * mm, "end": v(6.91, 11.35) * mm});
            skLineSegment(sketch, "E584", {"start": v(7.37, 11.1) * mm, "end": v(7.11, 11.25) * mm});
            skArc(sketch, "E585", {"start": v(7.37, 11.1) * mm, "mid": v(7.72, 11.07) * mm, "end": v(8.01, 11.27) * mm});
            skArc(sketch, "E586", {"start": v(8.24, 11.59) * mm, "mid": v(8.12, 11.43) * mm, "end": v(8.01, 11.27) * mm});
            skArc(sketch, "E587", {"start": v(8.24, 11.59) * mm, "mid": v(8.34, 11.92) * mm, "end": v(8.2, 12.25) * mm});
            skLineSegment(sketch, "E588", {"start": v(7.28, 13.95) * mm, "end": v(7.25, 14.4) * mm});
            skLineSegment(sketch, "E589", {"start": v(7.35, 13.54) * mm, "end": v(7.28, 13.95) * mm});
            skLineSegment(sketch, "E590", {"start": v(7.44, 13.23) * mm, "end": v(7.35, 13.54) * mm});
            skLineSegment(sketch, "E591", {"start": v(7.55, 12.97) * mm, "end": v(7.44, 13.23) * mm});
            skLineSegment(sketch, "E592", {"start": v(7.66, 12.78) * mm, "end": v(7.55, 12.97) * mm});
            skLineSegment(sketch, "E593", {"start": v(7.7, 12.73) * mm, "end": v(7.66, 12.78) * mm});
            skLineSegment(sketch, "E594", {"start": v(7.74, 12.69) * mm, "end": v(7.7, 12.73) * mm});
            skLineSegment(sketch, "E595", {"start": v(7.82, 12.6) * mm, "end": v(7.74, 12.69) * mm});
            skLineSegment(sketch, "E596", {"start": v(7.99, 12.45) * mm, "end": v(7.82, 12.6) * mm});
            skLineSegment(sketch, "E597", {"start": v(8.2, 12.25) * mm, "end": v(7.99, 12.45) * mm});
            skArc(sketch, "E598", {"start": v(7.82, 14.81) * mm, "mid": v(7.53, 14.61) * mm, "end": v(7.25, 14.4) * mm});
            skLineSegment(sketch, "E599", {"start": v(8.24, 14.65) * mm, "end": v(7.82, 14.81) * mm});
            skLineSegment(sketch, "E600", {"start": v(8.6, 14.45) * mm, "end": v(8.24, 14.65) * mm});
            skLineSegment(sketch, "E601", {"start": v(8.87, 14.27) * mm, "end": v(8.6, 14.45) * mm});
            skLineSegment(sketch, "E602", {"start": v(9.08, 14.1) * mm, "end": v(8.87, 14.27) * mm});
            skLineSegment(sketch, "E603", {"start": v(9.23, 13.92) * mm, "end": v(9.08, 14.1) * mm});
            skLineSegment(sketch, "E604", {"start": v(9.27, 13.86) * mm, "end": v(9.23, 13.92) * mm});
            skLineSegment(sketch, "E605", {"start": v(9.3, 13.82) * mm, "end": v(9.27, 13.86) * mm});
            skLineSegment(sketch, "E606", {"start": v(9.35, 13.71) * mm, "end": v(9.3, 13.82) * mm});
            skLineSegment(sketch, "E607", {"start": v(9.45, 13.5) * mm, "end": v(9.35, 13.71) * mm});
            skLineSegment(sketch, "E608", {"start": v(9.57, 13.25) * mm, "end": v(9.45, 13.5) * mm});
            skArc(sketch, "E609", {"start": v(9.57, 13.25) * mm, "mid": v(9.83, 13) * mm, "end": v(10.19, 13) * mm});
            skArc(sketch, "E610", {"start": v(10.56, 13.12) * mm, "mid": v(10.37, 13.07) * mm, "end": v(10.19, 13) * mm});
            skArc(sketch, "E611", {"start": v(10.56, 13.12) * mm, "mid": v(10.84, 13.33) * mm, "end": v(10.91, 13.68) * mm});
            skLineSegment(sketch, "E612", {"start": v(11.17, 15.6) * mm, "end": v(11.4, 15.98) * mm});
            skLineSegment(sketch, "E613", {"start": v(-5.02, 7.87) * mm, "end": v(-4.97, 7.85) * mm});
            skLineSegment(sketch, "E614", {"start": v(-5.05, 7.88) * mm, "end": v(-5.02, 7.87) * mm});
            skLineSegment(sketch, "E615", {"start": v(-5.11, 7.9) * mm, "end": v(-5.05, 7.88) * mm});
            skLineSegment(sketch, "E616", {"start": v(-5.27, 7.92) * mm, "end": v(-5.11, 7.9) * mm});
            skLineSegment(sketch, "E617", {"start": v(-5.6, 7.98) * mm, "end": v(-5.27, 7.92) * mm});
            skLineSegment(sketch, "E618", {"start": v(-6, 8.06) * mm, "end": v(-5.6, 7.98) * mm});
            skArc(sketch, "E619", {"start": v(-3.86, 5.66) * mm, "mid": v(-3.7, 6.03) * mm, "end": v(-3.55, 6.41) * mm});
            skLineSegment(sketch, "E620", {"start": v(-4.35, 5.55) * mm, "end": v(-3.86, 5.66) * mm});
            skLineSegment(sketch, "E621", {"start": v(-4.8, 5.5) * mm, "end": v(-4.35, 5.55) * mm});
            skLineSegment(sketch, "E622", {"start": v(-5.23, 5.5) * mm, "end": v(-4.8, 5.5) * mm});
            skLineSegment(sketch, "E623", {"start": v(-5.6, 5.56) * mm, "end": v(-5.23, 5.5) * mm});
            skLineSegment(sketch, "E624", {"start": v(-5.88, 5.65) * mm, "end": v(-5.6, 5.56) * mm});
            skLineSegment(sketch, "E625", {"start": v(-5.93, 5.67) * mm, "end": v(-5.88, 5.65) * mm});
            skLineSegment(sketch, "E626", {"start": v(-5.96, 5.69) * mm, "end": v(-5.93, 5.67) * mm});
            skLineSegment(sketch, "E627", {"start": v(-6.01, 5.72) * mm, "end": v(-5.96, 5.69) * mm});
            skLineSegment(sketch, "E628", {"start": v(-6.14, 5.8) * mm, "end": v(-6.01, 5.72) * mm});
            skLineSegment(sketch, "E629", {"start": v(-6.41, 6) * mm, "end": v(-6.14, 5.8) * mm});
            skLineSegment(sketch, "E630", {"start": v(-6.76, 6.24) * mm, "end": v(-6.41, 6) * mm});
            skArc(sketch, "E631", {"start": v(-6.76, 6.24) * mm, "mid": v(-7.18, 6.34) * mm, "end": v(-7.56, 6.15) * mm});
            skLineSegment(sketch, "E632", {"start": v(15.7, 12.6) * mm, "end": v(15.78, 12.69) * mm});
            skLineSegment(sketch, "E633", {"start": v(15.78, 12.69) * mm, "end": v(15.82, 12.73) * mm});
            skLineSegment(sketch, "E634", {"start": v(15.82, 12.73) * mm, "end": v(15.86, 12.78) * mm});
            skLineSegment(sketch, "E635", {"start": v(15.86, 12.78) * mm, "end": v(15.98, 12.97) * mm});
            skLineSegment(sketch, "E636", {"start": v(15.98, 12.97) * mm, "end": v(16.09, 13.23) * mm});
            skLineSegment(sketch, "E637", {"start": v(16.09, 13.23) * mm, "end": v(16.18, 13.54) * mm});
            skLineSegment(sketch, "E638", {"start": v(16.18, 13.54) * mm, "end": v(16.25, 13.95) * mm});
            skLineSegment(sketch, "E639", {"start": v(16.25, 13.95) * mm, "end": v(16.27, 14.4) * mm});
            skArc(sketch, "E640", {"start": v(16.27, 14.4) * mm, "mid": v(16, 14.61) * mm, "end": v(15.7, 14.81) * mm});
            skLineSegment(sketch, "E641", {"start": v(13.95, 13.25) * mm, "end": v(14.08, 13.5) * mm});
            skLineSegment(sketch, "E642", {"start": v(14.08, 13.5) * mm, "end": v(14.18, 13.71) * mm});
            skLineSegment(sketch, "E643", {"start": v(14.18, 13.71) * mm, "end": v(14.23, 13.82) * mm});
            skLineSegment(sketch, "E644", {"start": v(14.23, 13.82) * mm, "end": v(14.26, 13.86) * mm});
            skLineSegment(sketch, "E645", {"start": v(14.26, 13.86) * mm, "end": v(14.3, 13.92) * mm});
            skLineSegment(sketch, "E646", {"start": v(14.3, 13.92) * mm, "end": v(14.44, 14.1) * mm});
            skLineSegment(sketch, "E647", {"start": v(14.44, 14.1) * mm, "end": v(14.65, 14.27) * mm});
            skLineSegment(sketch, "E648", {"start": v(14.65, 14.27) * mm, "end": v(14.92, 14.45) * mm});
            skLineSegment(sketch, "E649", {"start": v(14.92, 14.45) * mm, "end": v(15.28, 14.65) * mm});
            skLineSegment(sketch, "E650", {"start": v(15.28, 14.65) * mm, "end": v(15.7, 14.81) * mm});
            skArc(sketch, "E651", {"start": v(13.33, 13) * mm, "mid": v(13.7, 13) * mm, "end": v(13.95, 13.25) * mm});
            skArc(sketch, "E652", {"start": v(13.33, 13) * mm, "mid": v(13.15, 13.07) * mm, "end": v(12.97, 13.12) * mm});
            skArc(sketch, "E653", {"start": v(-10.62, 7.3) * mm, "mid": v(-9.82, 7.52) * mm, "end": v(-9.24, 8.1) * mm});
            skArc(sketch, "E654", {"start": v(-10.62, 10.3) * mm, "mid": v(-11.32, 10.12) * mm, "end": v(-11.84, 9.6) * mm});
            skLineSegment(sketch, "E655", {"start": v(-10.62, 10.3) * mm, "end": v(-10.62, 10.5) * mm});
            skLineSegment(sketch, "E656", {"start": v(-11.84, 9.6) * mm, "end": v(-12.01, 9.7) * mm});
            skLineSegment(sketch, "E657", {"start": v(-11.84, 8.2) * mm, "end": v(-12.01, 8.1) * mm});
            skLineSegment(sketch, "E658", {"start": v(-10.62, 7.5) * mm, "end": v(-10.62, 7.3) * mm});
            skLineSegment(sketch, "E659", {"start": v(-9.41, 8.2) * mm, "end": v(-9.24, 8.1) * mm});
            skLineSegment(sketch, "E660", {"start": v(-9.41, 9.6) * mm, "end": v(-9.24, 9.7) * mm});
            skArc(sketch, "E661", {"start": v(-11.84, 8.2) * mm, "mid": v(-11.32, 7.7) * mm, "end": v(-10.62, 7.5) * mm});
            skArc(sketch, "E662", {"start": v(-9.41, 8.2) * mm, "mid": v(-9.22, 8.9) * mm, "end": v(-9.41, 9.6) * mm});
            skArc(sketch, "E663", {"start": v(-9.24, 9.7) * mm, "mid": v(-9.82, 10.29) * mm, "end": v(-10.62, 10.5) * mm});
            skArc(sketch, "E664", {"start": v(-12.01, 9.7) * mm, "mid": v(-12.22, 8.9) * mm, "end": v(-12.01, 8.1) * mm});
            skArc(sketch, "E665", {"start": v(11.76, 7.19) * mm, "mid": v(12.56, 7.4) * mm, "end": v(13.15, 7.99) * mm});
            skArc(sketch, "E666", {"start": v(11.76, 10.19) * mm, "mid": v(11.06, 10) * mm, "end": v(10.55, 9.49) * mm});
            skLineSegment(sketch, "E667", {"start": v(11.76, 10.19) * mm, "end": v(11.76, 10.39) * mm});
            skLineSegment(sketch, "E668", {"start": v(10.55, 9.49) * mm, "end": v(10.38, 9.59) * mm});
            skLineSegment(sketch, "E669", {"start": v(10.55, 8.09) * mm, "end": v(10.38, 7.99) * mm});
            skLineSegment(sketch, "E670", {"start": v(11.76, 7.39) * mm, "end": v(11.76, 7.19) * mm});
            skLineSegment(sketch, "E671", {"start": v(12.97, 8.09) * mm, "end": v(13.15, 7.99) * mm});
            skLineSegment(sketch, "E672", {"start": v(12.97, 9.49) * mm, "end": v(13.15, 9.59) * mm});
            skArc(sketch, "E673", {"start": v(10.55, 8.09) * mm, "mid": v(11.06, 7.57) * mm, "end": v(11.76, 7.39) * mm});
            skArc(sketch, "E674", {"start": v(12.97, 8.09) * mm, "mid": v(13.16, 8.79) * mm, "end": v(12.97, 9.49) * mm});
            skArc(sketch, "E675", {"start": v(13.15, 9.59) * mm, "mid": v(12.56, 10.17) * mm, "end": v(11.76, 10.39) * mm});
            skArc(sketch, "E676", {"start": v(10.38, 9.59) * mm, "mid": v(10.16, 8.79) * mm, "end": v(10.38, 7.99) * mm});
            skArc(sketch, "E677", {"start": v(-7.57, -11.77) * mm, "mid": v(-7.99, -11.67) * mm, "end": v(-8.37, -11.86) * mm});
            skLineSegment(sketch, "E678", {"start": v(-7.57, -11.77) * mm, "end": v(-7.22, -12.01) * mm});
            skLineSegment(sketch, "E679", {"start": v(-7.22, -12.01) * mm, "end": v(-6.95, -12.2) * mm});
            skLineSegment(sketch, "E680", {"start": v(-6.95, -12.2) * mm, "end": v(-6.82, -12.29) * mm});
            skLineSegment(sketch, "E681", {"start": v(-6.82, -12.29) * mm, "end": v(-6.77, -12.32) * mm});
            skLineSegment(sketch, "E682", {"start": v(-6.77, -12.32) * mm, "end": v(-6.73, -12.34) * mm});
            skLineSegment(sketch, "E683", {"start": v(-6.73, -12.34) * mm, "end": v(-6.69, -12.36) * mm});
            skLineSegment(sketch, "E684", {"start": v(-6.69, -12.36) * mm, "end": v(-6.4, -12.45) * mm});
            skLineSegment(sketch, "E685", {"start": v(-6.4, -12.45) * mm, "end": v(-6.04, -12.5) * mm});
            skLineSegment(sketch, "E686", {"start": v(-6.04, -12.5) * mm, "end": v(-5.62, -12.5) * mm});
            skLineSegment(sketch, "E687", {"start": v(-5.62, -12.5) * mm, "end": v(-5.16, -12.45) * mm});
            skLineSegment(sketch, "E688", {"start": v(-5.16, -12.45) * mm, "end": v(-4.67, -12.34) * mm});
            skArc(sketch, "E689", {"start": v(-4.67, -12.34) * mm, "mid": v(-4.5, -11.97) * mm, "end": v(-4.36, -11.6) * mm});
            skLineSegment(sketch, "E690", {"start": v(-6.82, -9.95) * mm, "end": v(-6.4, -10.03) * mm});
            skLineSegment(sketch, "E691", {"start": v(-6.4, -10.03) * mm, "end": v(-6.08, -10.09) * mm});
            skLineSegment(sketch, "E692", {"start": v(-6.08, -10.09) * mm, "end": v(-5.92, -10.12) * mm});
            skCircle(sketch, "E693", {"center": v(-12.99, 41.4) * mm, "radius": 3 * mm});
            skLineSegment(sketch, "E694", {"start": v(-5.92, -10.12) * mm, "end": v(-5.86, -10.13) * mm});
            skLineSegment(sketch, "E695", {"start": v(-5.86, -10.13) * mm, "end": v(-5.82, -10.14) * mm});
            skLineSegment(sketch, "E696", {"start": v(-5.82, -10.14) * mm, "end": v(-5.78, -10.16) * mm});
            skLineSegment(sketch, "E697", {"start": v(-5.78, -10.16) * mm, "end": v(-5.51, -10.3) * mm});
            skLineSegment(sketch, "E698", {"start": v(-5.51, -10.3) * mm, "end": v(-5.22, -10.52) * mm});
            skLineSegment(sketch, "E699", {"start": v(-5.22, -10.52) * mm, "end": v(-4.91, -10.81) * mm});
            skLineSegment(sketch, "E700", {"start": v(-4.91, -10.81) * mm, "end": v(-4.63, -11.17) * mm});
            skLineSegment(sketch, "E701", {"start": v(-4.63, -11.17) * mm, "end": v(-4.36, -11.6) * mm});
            skArc(sketch, "E702", {"start": v(-7.31, -9.32) * mm, "mid": v(-7.18, -9.73) * mm, "end": v(-6.82, -9.95) * mm});
            skArc(sketch, "E703", {"start": v(-7.31, -9.32) * mm, "mid": v(-7.3, -9.1) * mm, "end": v(-7.31, -8.89) * mm});
            skArc(sketch, "E704", {"start": v(-6.82, -8.26) * mm, "mid": v(-7.18, -8.48) * mm, "end": v(-7.31, -8.89) * mm});
            skLineSegment(sketch, "E705", {"start": v(-6.82, -8.26) * mm, "end": v(-6.4, -8.18) * mm});
            skLineSegment(sketch, "E706", {"start": v(-6.4, -8.18) * mm, "end": v(-6.08, -8.12) * mm});
            skLineSegment(sketch, "E707", {"start": v(-6.08, -8.12) * mm, "end": v(-5.92, -8.1) * mm});
            skLineSegment(sketch, "E708", {"start": v(-5.92, -8.1) * mm, "end": v(-5.86, -8.08) * mm});
            skLineSegment(sketch, "E709", {"start": v(-5.86, -8.08) * mm, "end": v(-5.82, -8.07) * mm});
            skLineSegment(sketch, "E710", {"start": v(-5.82, -8.07) * mm, "end": v(-5.78, -8.05) * mm});
            skLineSegment(sketch, "E711", {"start": v(-5.78, -8.05) * mm, "end": v(-5.51, -7.91) * mm});
            skLineSegment(sketch, "E712", {"start": v(-5.51, -7.91) * mm, "end": v(-5.22, -7.7) * mm});
            skLineSegment(sketch, "E713", {"start": v(-5.22, -7.7) * mm, "end": v(-4.91, -7.4) * mm});
            skLineSegment(sketch, "E714", {"start": v(-4.91, -7.4) * mm, "end": v(-4.63, -7.03) * mm});
            skLineSegment(sketch, "E715", {"start": v(-4.63, -7.03) * mm, "end": v(-4.36, -6.61) * mm});
            skArc(sketch, "E716", {"start": v(-4.36, -6.61) * mm, "mid": v(-4.5, -6.23) * mm, "end": v(-4.67, -5.86) * mm});
            skLineSegment(sketch, "E717", {"start": v(-7.57, -6.44) * mm, "end": v(-7.22, -6.2) * mm});
            skLineSegment(sketch, "E718", {"start": v(-7.22, -6.2) * mm, "end": v(-6.95, -6.01) * mm});
            skLineSegment(sketch, "E719", {"start": v(-6.95, -6.01) * mm, "end": v(-6.82, -5.92) * mm});
            skLineSegment(sketch, "E720", {"start": v(-6.82, -5.92) * mm, "end": v(-6.77, -5.89) * mm});
            skLineSegment(sketch, "E721", {"start": v(-6.77, -5.89) * mm, "end": v(-6.73, -5.87) * mm});
            skLineSegment(sketch, "E722", {"start": v(-6.73, -5.87) * mm, "end": v(-6.69, -5.85) * mm});
            skLineSegment(sketch, "E723", {"start": v(-6.69, -5.85) * mm, "end": v(-6.4, -5.76) * mm});
            skLineSegment(sketch, "E724", {"start": v(-6.4, -5.76) * mm, "end": v(-6.04, -5.7) * mm});
            skLineSegment(sketch, "E725", {"start": v(-6.04, -5.7) * mm, "end": v(-5.62, -5.7) * mm});
            skLineSegment(sketch, "E726", {"start": v(-5.62, -5.7) * mm, "end": v(-5.16, -5.75) * mm});
            skLineSegment(sketch, "E727", {"start": v(-5.16, -5.75) * mm, "end": v(-4.67, -5.86) * mm});
            skArc(sketch, "E728", {"start": v(-8.37, -6.35) * mm, "mid": v(-7.99, -6.54) * mm, "end": v(-7.57, -6.44) * mm});
            skArc(sketch, "E729", {"start": v(-8.37, -6.35) * mm, "mid": v(-8.52, -6.19) * mm, "end": v(-8.67, -6.04) * mm});
            skArc(sketch, "E730", {"start": v(-8.77, -5.24) * mm, "mid": v(-8.87, -5.66) * mm, "end": v(-8.67, -6.04) * mm});
            skLineSegment(sketch, "E731", {"start": v(-8.77, -5.24) * mm, "end": v(-8.52, -4.9) * mm});
            skLineSegment(sketch, "E732", {"start": v(-8.52, -4.9) * mm, "end": v(-8.34, -4.62) * mm});
            skLineSegment(sketch, "E733", {"start": v(-8.34, -4.62) * mm, "end": v(-8.25, -4.5) * mm});
            skLineSegment(sketch, "E734", {"start": v(-8.25, -4.5) * mm, "end": v(-8.22, -4.44) * mm});
            skLineSegment(sketch, "E735", {"start": v(-8.22, -4.44) * mm, "end": v(-8.2, -4.4) * mm});
            skLineSegment(sketch, "E736", {"start": v(-8.2, -4.4) * mm, "end": v(-8.18, -4.36) * mm});
            skLineSegment(sketch, "E737", {"start": v(-8.18, -4.36) * mm, "end": v(-8.1, -4.08) * mm});
            skLineSegment(sketch, "E738", {"start": v(-8.1, -4.08) * mm, "end": v(-8.04, -3.7) * mm});
            skLineSegment(sketch, "E739", {"start": v(-8.04, -3.7) * mm, "end": v(-8.03, -3.29) * mm});
            skLineSegment(sketch, "E740", {"start": v(-8.03, -3.29) * mm, "end": v(-8.08, -2.83) * mm});
            skLineSegment(sketch, "E741", {"start": v(-8.08, -2.83) * mm, "end": v(-8.2, -2.34) * mm});
            skArc(sketch, "E742", {"start": v(-8.2, -2.34) * mm, "mid": v(-8.56, -2.18) * mm, "end": v(-8.94, -2.03) * mm});
            skLineSegment(sketch, "E743", {"start": v(-10.59, -4.49) * mm, "end": v(-10.51, -4.07) * mm});
            skLineSegment(sketch, "E744", {"start": v(-10.51, -4.07) * mm, "end": v(-10.45, -3.75) * mm});
            skLineSegment(sketch, "E745", {"start": v(-10.45, -3.75) * mm, "end": v(-10.42, -3.59) * mm});
            skLineSegment(sketch, "E746", {"start": v(-10.42, -3.59) * mm, "end": v(-10.4, -3.53) * mm});
            skLineSegment(sketch, "E747", {"start": v(-10.4, -3.53) * mm, "end": v(-10.4, -3.5) * mm});
            skLineSegment(sketch, "E748", {"start": v(-10.4, -3.5) * mm, "end": v(-10.38, -3.45) * mm});
            skLineSegment(sketch, "E749", {"start": v(-10.38, -3.45) * mm, "end": v(-10.24, -3.19) * mm});
            skLineSegment(sketch, "E750", {"start": v(-10.24, -3.19) * mm, "end": v(-10.02, -2.89) * mm});
            skLineSegment(sketch, "E751", {"start": v(-10.02, -2.89) * mm, "end": v(-9.72, -2.59) * mm});
            skLineSegment(sketch, "E752", {"start": v(-9.72, -2.59) * mm, "end": v(-9.36, -2.3) * mm});
            skLineSegment(sketch, "E753", {"start": v(-9.36, -2.3) * mm, "end": v(-8.94, -2.03) * mm});
            skArc(sketch, "E754", {"start": v(-11.21, -4.99) * mm, "mid": v(-10.8, -4.86) * mm, "end": v(-10.59, -4.49) * mm});
            skArc(sketch, "E755", {"start": v(-11.21, -4.99) * mm, "mid": v(-11.43, -4.98) * mm, "end": v(-11.65, -4.99) * mm});
            skArc(sketch, "E756", {"start": v(-12.28, -4.49) * mm, "mid": v(-12.06, -4.86) * mm, "end": v(-11.65, -4.99) * mm});
            skLineSegment(sketch, "E757", {"start": v(-12.28, -4.49) * mm, "end": v(-12.35, -4.07) * mm});
            skLineSegment(sketch, "E758", {"start": v(-12.35, -4.07) * mm, "end": v(-12.41, -3.75) * mm});
            skLineSegment(sketch, "E759", {"start": v(-12.41, -3.75) * mm, "end": v(-12.44, -3.59) * mm});
            skLineSegment(sketch, "E760", {"start": v(-12.44, -3.59) * mm, "end": v(-12.46, -3.53) * mm});
            skLineSegment(sketch, "E761", {"start": v(-12.46, -3.53) * mm, "end": v(-12.47, -3.5) * mm});
            skLineSegment(sketch, "E762", {"start": v(-12.47, -3.5) * mm, "end": v(-12.49, -3.45) * mm});
            skLineSegment(sketch, "E763", {"start": v(-12.49, -3.45) * mm, "end": v(-12.62, -3.19) * mm});
            skLineSegment(sketch, "E764", {"start": v(-12.62, -3.19) * mm, "end": v(-12.85, -2.89) * mm});
            skLineSegment(sketch, "E765", {"start": v(-12.85, -2.89) * mm, "end": v(-13.14, -2.59) * mm});
            skLineSegment(sketch, "E766", {"start": v(-13.14, -2.59) * mm, "end": v(-13.5, -2.3) * mm});
            skLineSegment(sketch, "E767", {"start": v(-13.5, -2.3) * mm, "end": v(-13.92, -2.03) * mm});
            skArc(sketch, "E768", {"start": v(-13.92, -2.03) * mm, "mid": v(-14.3, -2.18) * mm, "end": v(-14.67, -2.34) * mm});
            skLineSegment(sketch, "E769", {"start": v(-14.1, -5.24) * mm, "end": v(-14.34, -4.9) * mm});
            skLineSegment(sketch, "E770", {"start": v(-14.34, -4.9) * mm, "end": v(-14.53, -4.62) * mm});
            skLineSegment(sketch, "E771", {"start": v(-14.53, -4.62) * mm, "end": v(-14.62, -4.5) * mm});
            skLineSegment(sketch, "E772", {"start": v(-14.62, -4.5) * mm, "end": v(-14.65, -4.44) * mm});
            skLineSegment(sketch, "E773", {"start": v(-14.65, -4.44) * mm, "end": v(-14.67, -4.4) * mm});
            skLineSegment(sketch, "E774", {"start": v(-14.67, -4.4) * mm, "end": v(-14.69, -4.36) * mm});
            skLineSegment(sketch, "E775", {"start": v(-14.69, -4.36) * mm, "end": v(-14.78, -4.08) * mm});
            skLineSegment(sketch, "E776", {"start": v(-14.78, -4.08) * mm, "end": v(-14.83, -3.7) * mm});
            skLineSegment(sketch, "E777", {"start": v(-14.83, -3.7) * mm, "end": v(-14.83, -3.29) * mm});
            skLineSegment(sketch, "E778", {"start": v(-14.83, -3.29) * mm, "end": v(-14.78, -2.83) * mm});
            skLineSegment(sketch, "E779", {"start": v(-14.78, -2.83) * mm, "end": v(-14.67, -2.34) * mm});
            skArc(sketch, "E780", {"start": v(-14.2, -6.04) * mm, "mid": v(-14, -5.66) * mm, "end": v(-14.1, -5.24) * mm});
            skArc(sketch, "E781", {"start": v(-14.2, -6.04) * mm, "mid": v(-14.35, -6.19) * mm, "end": v(-14.5, -6.35) * mm});
            skArc(sketch, "E782", {"start": v(-15.3, -6.44) * mm, "mid": v(-14.88, -6.54) * mm, "end": v(-14.5, -6.35) * mm});
            skLineSegment(sketch, "E783", {"start": v(-15.3, -6.44) * mm, "end": v(-15.64, -6.2) * mm});
            skLineSegment(sketch, "E784", {"start": v(-15.64, -6.2) * mm, "end": v(-15.91, -6.01) * mm});
            skLineSegment(sketch, "E785", {"start": v(-15.91, -6.01) * mm, "end": v(-16.05, -5.92) * mm});
            skLineSegment(sketch, "E786", {"start": v(-16.05, -5.92) * mm, "end": v(-16.1, -5.89) * mm});
            skLineSegment(sketch, "E787", {"start": v(-16.1, -5.89) * mm, "end": v(-16.13, -5.87) * mm});
            skLineSegment(sketch, "E788", {"start": v(-16.13, -5.87) * mm, "end": v(-16.18, -5.85) * mm});
            skLineSegment(sketch, "E789", {"start": v(-16.18, -5.85) * mm, "end": v(-16.46, -5.76) * mm});
            skLineSegment(sketch, "E790", {"start": v(-16.46, -5.76) * mm, "end": v(-16.83, -5.7) * mm});
            skLineSegment(sketch, "E791", {"start": v(-16.83, -5.7) * mm, "end": v(-17.25, -5.7) * mm});
            skLineSegment(sketch, "E792", {"start": v(-17.25, -5.7) * mm, "end": v(-17.71, -5.75) * mm});
            skLineSegment(sketch, "E793", {"start": v(-17.71, -5.75) * mm, "end": v(-18.2, -5.86) * mm});
            skArc(sketch, "E794", {"start": v(-18.2, -5.86) * mm, "mid": v(-18.36, -6.23) * mm, "end": v(-18.5, -6.61) * mm});
            skLineSegment(sketch, "E795", {"start": v(-16.05, -8.26) * mm, "end": v(-16.47, -8.18) * mm});
            skLineSegment(sketch, "E796", {"start": v(-16.47, -8.18) * mm, "end": v(-16.79, -8.12) * mm});
            skLineSegment(sketch, "E797", {"start": v(-16.79, -8.12) * mm, "end": v(-16.95, -8.1) * mm});
            skLineSegment(sketch, "E798", {"start": v(-16.95, -8.1) * mm, "end": v(-17, -8.08) * mm});
            skLineSegment(sketch, "E799", {"start": v(-17, -8.08) * mm, "end": v(-17.04, -8.07) * mm});
            skLineSegment(sketch, "E800", {"start": v(-17.04, -8.07) * mm, "end": v(-17.09, -8.05) * mm});
            skLineSegment(sketch, "E801", {"start": v(-17.09, -8.05) * mm, "end": v(-17.35, -7.91) * mm});
            skLineSegment(sketch, "E802", {"start": v(-17.35, -7.91) * mm, "end": v(-17.65, -7.7) * mm});
            skLineSegment(sketch, "E803", {"start": v(-17.65, -7.7) * mm, "end": v(-17.95, -7.4) * mm});
            skLineSegment(sketch, "E804", {"start": v(-17.95, -7.4) * mm, "end": v(-18.24, -7.03) * mm});
            skLineSegment(sketch, "E805", {"start": v(-18.24, -7.03) * mm, "end": v(-18.5, -6.61) * mm});
            skArc(sketch, "E806", {"start": v(-15.55, -8.89) * mm, "mid": v(-15.68, -8.48) * mm, "end": v(-16.05, -8.26) * mm});
            skArc(sketch, "E807", {"start": v(-15.55, -8.89) * mm, "mid": v(-15.56, -9.1) * mm, "end": v(-15.55, -9.32) * mm});
            skArc(sketch, "E808", {"start": v(-16.05, -9.95) * mm, "mid": v(-15.68, -9.73) * mm, "end": v(-15.55, -9.32) * mm});
            skLineSegment(sketch, "E809", {"start": v(-16.05, -9.95) * mm, "end": v(-16.47, -10.03) * mm});
            skLineSegment(sketch, "E810", {"start": v(-16.47, -10.03) * mm, "end": v(-16.79, -10.09) * mm});
            skLineSegment(sketch, "E811", {"start": v(-16.79, -10.09) * mm, "end": v(-16.95, -10.12) * mm});
            skLineSegment(sketch, "E812", {"start": v(-16.95, -10.12) * mm, "end": v(-17, -10.13) * mm});
            skLineSegment(sketch, "E813", {"start": v(-17, -10.13) * mm, "end": v(-17.04, -10.14) * mm});
            skLineSegment(sketch, "E814", {"start": v(-17.04, -10.14) * mm, "end": v(-17.09, -10.16) * mm});
            skLineSegment(sketch, "E815", {"start": v(-17.09, -10.16) * mm, "end": v(-17.35, -10.3) * mm});
            skLineSegment(sketch, "E816", {"start": v(-17.35, -10.3) * mm, "end": v(-17.65, -10.52) * mm});
            skLineSegment(sketch, "E817", {"start": v(-17.65, -10.52) * mm, "end": v(-17.95, -10.81) * mm});
            skLineSegment(sketch, "E818", {"start": v(-17.95, -10.81) * mm, "end": v(-18.24, -11.17) * mm});
            skLineSegment(sketch, "E819", {"start": v(-18.24, -11.17) * mm, "end": v(-18.5, -11.6) * mm});
            skArc(sketch, "E820", {"start": v(-18.5, -11.6) * mm, "mid": v(-18.36, -11.97) * mm, "end": v(-18.2, -12.34) * mm});
            skLineSegment(sketch, "E821", {"start": v(-15.3, -11.77) * mm, "end": v(-15.64, -12.01) * mm});
            skLineSegment(sketch, "E822", {"start": v(-15.64, -12.01) * mm, "end": v(-15.91, -12.2) * mm});
            skLineSegment(sketch, "E823", {"start": v(-15.91, -12.2) * mm, "end": v(-16.05, -12.29) * mm});
            skLineSegment(sketch, "E824", {"start": v(-16.05, -12.29) * mm, "end": v(-16.1, -12.32) * mm});
            skLineSegment(sketch, "E825", {"start": v(-16.1, -12.32) * mm, "end": v(-16.13, -12.34) * mm});
            skLineSegment(sketch, "E826", {"start": v(-16.13, -12.34) * mm, "end": v(-16.18, -12.36) * mm});
            skLineSegment(sketch, "E827", {"start": v(-16.18, -12.36) * mm, "end": v(-16.46, -12.45) * mm});
            skLineSegment(sketch, "E828", {"start": v(-16.46, -12.45) * mm, "end": v(-16.83, -12.5) * mm});
            skLineSegment(sketch, "E829", {"start": v(-16.83, -12.5) * mm, "end": v(-17.25, -12.5) * mm});
            skLineSegment(sketch, "E830", {"start": v(-17.25, -12.5) * mm, "end": v(-17.71, -12.45) * mm});
            skLineSegment(sketch, "E831", {"start": v(-17.71, -12.45) * mm, "end": v(-18.2, -12.34) * mm});
            skArc(sketch, "E832", {"start": v(-14.5, -11.86) * mm, "mid": v(-14.88, -11.67) * mm, "end": v(-15.3, -11.77) * mm});
            skArc(sketch, "E833", {"start": v(-14.5, -11.86) * mm, "mid": v(-14.35, -12.02) * mm, "end": v(-14.2, -12.17) * mm});
            skArc(sketch, "E834", {"start": v(-14.1, -12.97) * mm, "mid": v(-14, -12.55) * mm, "end": v(-14.2, -12.17) * mm});
            skLineSegment(sketch, "E835", {"start": v(-14.1, -12.97) * mm, "end": v(-14.34, -13.32) * mm});
            skLineSegment(sketch, "E836", {"start": v(-14.34, -13.32) * mm, "end": v(-14.53, -13.59) * mm});
            skLineSegment(sketch, "E837", {"start": v(-14.53, -13.59) * mm, "end": v(-14.62, -13.72) * mm});
            skLineSegment(sketch, "E838", {"start": v(-14.62, -13.72) * mm, "end": v(-14.65, -13.77) * mm});
            skLineSegment(sketch, "E839", {"start": v(-14.65, -13.77) * mm, "end": v(-14.67, -13.8) * mm});
            skLineSegment(sketch, "E840", {"start": v(-14.67, -13.8) * mm, "end": v(-14.69, -13.85) * mm});
            skLineSegment(sketch, "E841", {"start": v(-14.69, -13.85) * mm, "end": v(-14.78, -14.13) * mm});
            skLineSegment(sketch, "E842", {"start": v(-14.78, -14.13) * mm, "end": v(-14.83, -14.5) * mm});
            skLineSegment(sketch, "E843", {"start": v(-14.83, -14.5) * mm, "end": v(-14.83, -14.92) * mm});
            skLineSegment(sketch, "E844", {"start": v(-14.83, -14.92) * mm, "end": v(-14.78, -15.38) * mm});
            skLineSegment(sketch, "E845", {"start": v(-14.78, -15.38) * mm, "end": v(-14.67, -15.87) * mm});
            skArc(sketch, "E846", {"start": v(-14.67, -15.87) * mm, "mid": v(-14.3, -16.03) * mm, "end": v(-13.92, -16.18) * mm});
            skLineSegment(sketch, "E847", {"start": v(-12.28, -13.72) * mm, "end": v(-12.35, -14.14) * mm});
            skLineSegment(sketch, "E848", {"start": v(-12.35, -14.14) * mm, "end": v(-12.41, -14.46) * mm});
            skLineSegment(sketch, "E849", {"start": v(-12.41, -14.46) * mm, "end": v(-12.44, -14.62) * mm});
            skLineSegment(sketch, "E850", {"start": v(-12.44, -14.62) * mm, "end": v(-12.46, -14.67) * mm});
            skLineSegment(sketch, "E851", {"start": v(-12.46, -14.67) * mm, "end": v(-12.47, -14.71) * mm});
            skLineSegment(sketch, "E852", {"start": v(-12.47, -14.71) * mm, "end": v(-12.49, -14.76) * mm});
            skLineSegment(sketch, "E853", {"start": v(-12.49, -14.76) * mm, "end": v(-12.62, -15.02) * mm});
            skLineSegment(sketch, "E854", {"start": v(-12.62, -15.02) * mm, "end": v(-12.85, -15.32) * mm});
            skLineSegment(sketch, "E855", {"start": v(-12.85, -15.32) * mm, "end": v(-13.14, -15.62) * mm});
            skLineSegment(sketch, "E856", {"start": v(-13.14, -15.62) * mm, "end": v(-13.5, -15.91) * mm});
            skLineSegment(sketch, "E857", {"start": v(-13.5, -15.91) * mm, "end": v(-13.92, -16.18) * mm});
            skArc(sketch, "E858", {"start": v(-11.65, -13.22) * mm, "mid": v(-12.06, -13.35) * mm, "end": v(-12.28, -13.72) * mm});
            skArc(sketch, "E859", {"start": v(-11.65, -13.22) * mm, "mid": v(-11.43, -13.23) * mm, "end": v(-11.21, -13.22) * mm});
            skArc(sketch, "E860", {"start": v(-10.59, -13.72) * mm, "mid": v(-10.8, -13.35) * mm, "end": v(-11.21, -13.22) * mm});
            skLineSegment(sketch, "E861", {"start": v(-10.59, -13.72) * mm, "end": v(-10.51, -14.14) * mm});
            skLineSegment(sketch, "E862", {"start": v(-10.51, -14.14) * mm, "end": v(-10.45, -14.46) * mm});
            skLineSegment(sketch, "E863", {"start": v(-10.45, -14.46) * mm, "end": v(-10.42, -14.62) * mm});
            skLineSegment(sketch, "E864", {"start": v(-10.42, -14.62) * mm, "end": v(-10.4, -14.67) * mm});
            skLineSegment(sketch, "E865", {"start": v(-10.4, -14.67) * mm, "end": v(-10.4, -14.71) * mm});
            skLineSegment(sketch, "E866", {"start": v(-10.4, -14.71) * mm, "end": v(-10.38, -14.76) * mm});
            skLineSegment(sketch, "E867", {"start": v(-10.38, -14.76) * mm, "end": v(-10.24, -15.02) * mm});
            skLineSegment(sketch, "E868", {"start": v(-10.24, -15.02) * mm, "end": v(-10.02, -15.32) * mm});
            skLineSegment(sketch, "E869", {"start": v(-10.02, -15.32) * mm, "end": v(-9.72, -15.62) * mm});
            skLineSegment(sketch, "E870", {"start": v(-9.72, -15.62) * mm, "end": v(-9.36, -15.91) * mm});
            skLineSegment(sketch, "E871", {"start": v(-9.36, -15.91) * mm, "end": v(-8.94, -16.18) * mm});
            skArc(sketch, "E872", {"start": v(-8.94, -16.18) * mm, "mid": v(-8.56, -16.03) * mm, "end": v(-8.2, -15.87) * mm});
            skLineSegment(sketch, "E873", {"start": v(-8.77, -12.97) * mm, "end": v(-8.52, -13.32) * mm});
            skLineSegment(sketch, "E874", {"start": v(-8.52, -13.32) * mm, "end": v(-8.34, -13.59) * mm});
            skLineSegment(sketch, "E875", {"start": v(-8.34, -13.59) * mm, "end": v(-8.25, -13.72) * mm});
            skLineSegment(sketch, "E876", {"start": v(-8.25, -13.72) * mm, "end": v(-8.22, -13.77) * mm});
            skLineSegment(sketch, "E877", {"start": v(-8.22, -13.77) * mm, "end": v(-8.2, -13.8) * mm});
            skLineSegment(sketch, "E878", {"start": v(-8.2, -13.8) * mm, "end": v(-8.18, -13.85) * mm});
            skLineSegment(sketch, "E879", {"start": v(-8.18, -13.85) * mm, "end": v(-8.1, -14.13) * mm});
            skLineSegment(sketch, "E880", {"start": v(-8.1, -14.13) * mm, "end": v(-8.04, -14.5) * mm});
            skLineSegment(sketch, "E881", {"start": v(-8.04, -14.5) * mm, "end": v(-8.03, -14.92) * mm});
            skLineSegment(sketch, "E882", {"start": v(-8.03, -14.92) * mm, "end": v(-8.08, -15.38) * mm});
            skLineSegment(sketch, "E883", {"start": v(-8.08, -15.38) * mm, "end": v(-8.2, -15.87) * mm});
            skArc(sketch, "E884", {"start": v(-8.67, -12.17) * mm, "mid": v(-8.87, -12.55) * mm, "end": v(-8.77, -12.97) * mm});
            skArc(sketch, "E885", {"start": v(-8.67, -12.17) * mm, "mid": v(-8.52, -12.02) * mm, "end": v(-8.37, -11.86) * mm});
            skArc(sketch, "E886", {"start": v(11.8, -4.32) * mm, "mid": v(11.87, -4.67) * mm, "end": v(12.16, -4.89) * mm});
            skLineSegment(sketch, "E887", {"start": v(11.8, -4.32) * mm, "end": v(11.86, -4.04) * mm});
            skLineSegment(sketch, "E888", {"start": v(11.86, -4.04) * mm, "end": v(11.9, -3.82) * mm});
            skLineSegment(sketch, "E889", {"start": v(11.9, -3.82) * mm, "end": v(11.91, -3.7) * mm});
            skLineSegment(sketch, "E890", {"start": v(11.91, -3.7) * mm, "end": v(11.92, -3.65) * mm});
            skLineSegment(sketch, "E891", {"start": v(11.92, -3.65) * mm, "end": v(11.92, -3.58) * mm});
            skLineSegment(sketch, "E892", {"start": v(11.92, -3.58) * mm, "end": v(11.9, -3.36) * mm});
            skLineSegment(sketch, "E893", {"start": v(11.9, -3.36) * mm, "end": v(11.84, -3.08) * mm});
            skLineSegment(sketch, "E894", {"start": v(11.84, -3.08) * mm, "end": v(11.73, -2.78) * mm});
            skLineSegment(sketch, "E895", {"start": v(11.73, -2.78) * mm, "end": v(11.55, -2.41) * mm});
            skLineSegment(sketch, "E896", {"start": v(11.55, -2.41) * mm, "end": v(11.3, -2.03) * mm});
            skArc(sketch, "E897", {"start": v(11.3, -2.03) * mm, "mid": v(10.95, -2.02) * mm, "end": v(10.6, -2.03) * mm});
            skLineSegment(sketch, "E898", {"start": v(10.1, -4.32) * mm, "end": v(10.05, -4.04) * mm});
            skLineSegment(sketch, "E899", {"start": v(10.05, -4.04) * mm, "end": v(10.01, -3.82) * mm});
            skLineSegment(sketch, "E900", {"start": v(10.01, -3.82) * mm, "end": v(10, -3.7) * mm});
            skLineSegment(sketch, "E901", {"start": v(10, -3.7) * mm, "end": v(9.99, -3.65) * mm});
            skLineSegment(sketch, "E902", {"start": v(9.99, -3.65) * mm, "end": v(9.98, -3.58) * mm});
            skLineSegment(sketch, "E903", {"start": v(9.98, -3.58) * mm, "end": v(10, -3.36) * mm});
            skLineSegment(sketch, "E904", {"start": v(10, -3.36) * mm, "end": v(10.07, -3.08) * mm});
            skLineSegment(sketch, "E905", {"start": v(10.07, -3.08) * mm, "end": v(10.17, -2.78) * mm});
            skLineSegment(sketch, "E906", {"start": v(10.17, -2.78) * mm, "end": v(10.36, -2.41) * mm});
            skLineSegment(sketch, "E907", {"start": v(10.36, -2.41) * mm, "end": v(10.6, -2.03) * mm});
            skArc(sketch, "E908", {"start": v(9.75, -4.89) * mm, "mid": v(10.03, -4.67) * mm, "end": v(10.1, -4.32) * mm});
            skArc(sketch, "E909", {"start": v(9.75, -4.89) * mm, "mid": v(9.56, -4.94) * mm, "end": v(9.38, -5) * mm});
            skArc(sketch, "E910", {"start": v(8.76, -4.76) * mm, "mid": v(9.03, -5) * mm, "end": v(9.38, -5) * mm});
            skLineSegment(sketch, "E911", {"start": v(8.76, -4.76) * mm, "end": v(8.64, -4.5) * mm});
            skLineSegment(sketch, "E912", {"start": v(8.64, -4.5) * mm, "end": v(8.54, -4.3) * mm});
            skLineSegment(sketch, "E913", {"start": v(8.54, -4.3) * mm, "end": v(8.48, -4.2) * mm});
            skLineSegment(sketch, "E914", {"start": v(8.48, -4.2) * mm, "end": v(8.46, -4.14) * mm});
            skLineSegment(sketch, "E915", {"start": v(8.46, -4.14) * mm, "end": v(8.42, -4.09) * mm});
            skLineSegment(sketch, "E916", {"start": v(8.42, -4.09) * mm, "end": v(8.27, -3.92) * mm});
            skLineSegment(sketch, "E917", {"start": v(8.27, -3.92) * mm, "end": v(8.06, -3.73) * mm});
            skLineSegment(sketch, "E918", {"start": v(8.06, -3.73) * mm, "end": v(7.8, -3.55) * mm});
            skLineSegment(sketch, "E919", {"start": v(7.8, -3.55) * mm, "end": v(7.43, -3.36) * mm});
            skLineSegment(sketch, "E920", {"start": v(7.43, -3.36) * mm, "end": v(7.01, -3.2) * mm});
            skArc(sketch, "E921", {"start": v(7.01, -3.2) * mm, "mid": v(6.72, -3.4) * mm, "end": v(6.44, -3.61) * mm});
            skLineSegment(sketch, "E922", {"start": v(7.39, -5.76) * mm, "end": v(7.18, -5.56) * mm});
            skLineSegment(sketch, "E923", {"start": v(7.18, -5.56) * mm, "end": v(7.02, -5.4) * mm});
            skLineSegment(sketch, "E924", {"start": v(7.02, -5.4) * mm, "end": v(6.93, -5.32) * mm});
            skLineSegment(sketch, "E925", {"start": v(6.93, -5.32) * mm, "end": v(6.9, -5.28) * mm});
            skLineSegment(sketch, "E926", {"start": v(6.9, -5.28) * mm, "end": v(6.85, -5.23) * mm});
            skLineSegment(sketch, "E927", {"start": v(6.85, -5.23) * mm, "end": v(6.74, -5.03) * mm});
            skLineSegment(sketch, "E928", {"start": v(6.74, -5.03) * mm, "end": v(6.63, -4.78) * mm});
            skLineSegment(sketch, "E929", {"start": v(6.63, -4.78) * mm, "end": v(6.54, -4.47) * mm});
            skLineSegment(sketch, "E930", {"start": v(6.54, -4.47) * mm, "end": v(6.47, -4.06) * mm});
            skLineSegment(sketch, "E931", {"start": v(6.47, -4.06) * mm, "end": v(6.44, -3.61) * mm});
            skArc(sketch, "E932", {"start": v(7.43, -6.42) * mm, "mid": v(7.54, -6.08) * mm, "end": v(7.39, -5.76) * mm});
            skArc(sketch, "E933", {"start": v(7.43, -6.42) * mm, "mid": v(7.31, -6.58) * mm, "end": v(7.2, -6.74) * mm});
            skArc(sketch, "E934", {"start": v(6.56, -6.9) * mm, "mid": v(6.91, -6.94) * mm, "end": v(7.2, -6.74) * mm});
            skLineSegment(sketch, "E935", {"start": v(6.56, -6.9) * mm, "end": v(6.3, -6.76) * mm});
            skLineSegment(sketch, "E936", {"start": v(6.3, -6.76) * mm, "end": v(6.1, -6.66) * mm});
            skLineSegment(sketch, "E937", {"start": v(6.1, -6.66) * mm, "end": v(6, -6.6) * mm});
            skLineSegment(sketch, "E938", {"start": v(6, -6.6) * mm, "end": v(5.95, -6.58) * mm});
            skLineSegment(sketch, "E939", {"start": v(5.95, -6.58) * mm, "end": v(5.89, -6.56) * mm});
            skLineSegment(sketch, "E940", {"start": v(5.89, -6.56) * mm, "end": v(5.67, -6.5) * mm});
            skLineSegment(sketch, "E941", {"start": v(5.67, -6.5) * mm, "end": v(5.39, -6.48) * mm});
            skLineSegment(sketch, "E942", {"start": v(5.39, -6.48) * mm, "end": v(5.07, -6.5) * mm});
            skLineSegment(sketch, "E943", {"start": v(5.07, -6.5) * mm, "end": v(4.66, -6.55) * mm});
            skLineSegment(sketch, "E944", {"start": v(4.66, -6.55) * mm, "end": v(4.22, -6.66) * mm});
            skArc(sketch, "E945", {"start": v(4.22, -6.66) * mm, "mid": v(4.1, -7) * mm, "end": v(4, -7.33) * mm});
            skLineSegment(sketch, "E946", {"start": v(6.03, -8.52) * mm, "end": v(5.75, -8.48) * mm});
            skLineSegment(sketch, "E947", {"start": v(5.75, -8.48) * mm, "end": v(5.52, -8.45) * mm});
            skLineSegment(sketch, "E948", {"start": v(5.52, -8.45) * mm, "end": v(5.4, -8.43) * mm});
            skLineSegment(sketch, "E949", {"start": v(5.4, -8.43) * mm, "end": v(5.35, -8.42) * mm});
            skLineSegment(sketch, "E950", {"start": v(5.35, -8.42) * mm, "end": v(5.29, -8.4) * mm});
            skLineSegment(sketch, "E951", {"start": v(5.29, -8.4) * mm, "end": v(5.08, -8.31) * mm});
            skLineSegment(sketch, "E952", {"start": v(5.08, -8.31) * mm, "end": v(4.84, -8.17) * mm});
            skLineSegment(sketch, "E953", {"start": v(4.84, -8.17) * mm, "end": v(4.59, -7.97) * mm});
            skLineSegment(sketch, "E954", {"start": v(4.59, -7.97) * mm, "end": v(4.3, -7.68) * mm});
            skLineSegment(sketch, "E955", {"start": v(4.3, -7.68) * mm, "end": v(4, -7.33) * mm});
            skArc(sketch, "E956", {"start": v(6.46, -9.03) * mm, "mid": v(6.34, -8.7) * mm, "end": v(6.03, -8.52) * mm});
            skArc(sketch, "E957", {"start": v(6.46, -9.03) * mm, "mid": v(6.45, -9.22) * mm, "end": v(6.46, -9.41) * mm});
            skArc(sketch, "E958", {"start": v(6.03, -9.92) * mm, "mid": v(6.34, -9.75) * mm, "end": v(6.46, -9.41) * mm});
            skLineSegment(sketch, "E959", {"start": v(6.03, -9.92) * mm, "end": v(5.75, -9.97) * mm});
            skCircle(sketch, "E960", {"center": v(-11.47, 28.21) * mm, "radius": 3 * mm});
            skLineSegment(sketch, "E961", {"start": v(5.75, -9.97) * mm, "end": v(5.52, -10) * mm});
            skLineSegment(sketch, "E962", {"start": v(5.52, -10) * mm, "end": v(5.4, -10.02) * mm});
            skLineSegment(sketch, "E963", {"start": v(5.4, -10.02) * mm, "end": v(5.35, -10.02) * mm});
            skLineSegment(sketch, "E964", {"start": v(5.35, -10.02) * mm, "end": v(5.29, -10.04) * mm});
            skLineSegment(sketch, "E965", {"start": v(5.29, -10.04) * mm, "end": v(5.08, -10.13) * mm});
            skLineSegment(sketch, "E966", {"start": v(5.08, -10.13) * mm, "end": v(4.84, -10.28) * mm});
            skLineSegment(sketch, "E967", {"start": v(4.84, -10.28) * mm, "end": v(4.59, -10.47) * mm});
            skLineSegment(sketch, "E968", {"start": v(4.59, -10.47) * mm, "end": v(4.3, -10.76) * mm});
            skLineSegment(sketch, "E969", {"start": v(4.3, -10.76) * mm, "end": v(4, -11.1) * mm});
            skArc(sketch, "E970", {"start": v(4, -11.1) * mm, "mid": v(4.1, -11.45) * mm, "end": v(4.22, -11.78) * mm});
            skLineSegment(sketch, "E971", {"start": v(6.56, -11.55) * mm, "end": v(6.3, -11.68) * mm});
            skLineSegment(sketch, "E972", {"start": v(6.3, -11.68) * mm, "end": v(6.1, -11.79) * mm});
            skLineSegment(sketch, "E973", {"start": v(6.1, -11.79) * mm, "end": v(6, -11.84) * mm});
            skLineSegment(sketch, "E974", {"start": v(6, -11.84) * mm, "end": v(5.95, -11.86) * mm});
            skLineSegment(sketch, "E975", {"start": v(5.95, -11.86) * mm, "end": v(5.89, -11.89) * mm});
            skLineSegment(sketch, "E976", {"start": v(5.89, -11.89) * mm, "end": v(5.67, -11.94) * mm});
            skLineSegment(sketch, "E977", {"start": v(5.67, -11.94) * mm, "end": v(5.39, -11.96) * mm});
            skLineSegment(sketch, "E978", {"start": v(5.39, -11.96) * mm, "end": v(5.07, -11.95) * mm});
            skLineSegment(sketch, "E979", {"start": v(5.07, -11.95) * mm, "end": v(4.66, -11.9) * mm});
            skLineSegment(sketch, "E980", {"start": v(4.66, -11.9) * mm, "end": v(4.22, -11.78) * mm});
            skArc(sketch, "E981", {"start": v(7.2, -11.7) * mm, "mid": v(6.91, -11.5) * mm, "end": v(6.56, -11.55) * mm});
            skArc(sketch, "E982", {"start": v(7.2, -11.7) * mm, "mid": v(7.31, -11.87) * mm, "end": v(7.43, -12.02) * mm});
            skArc(sketch, "E983", {"start": v(7.39, -12.68) * mm, "mid": v(7.54, -12.36) * mm, "end": v(7.43, -12.02) * mm});
            skLineSegment(sketch, "E984", {"start": v(7.39, -12.68) * mm, "end": v(7.18, -12.88) * mm});
            skLineSegment(sketch, "E985", {"start": v(7.18, -12.88) * mm, "end": v(7.02, -13.04) * mm});
            skLineSegment(sketch, "E986", {"start": v(7.02, -13.04) * mm, "end": v(6.93, -13.12) * mm});
            skLineSegment(sketch, "E987", {"start": v(6.93, -13.12) * mm, "end": v(6.9, -13.16) * mm});
            skLineSegment(sketch, "E988", {"start": v(6.9, -13.16) * mm, "end": v(6.85, -13.22) * mm});
            skLineSegment(sketch, "E989", {"start": v(6.85, -13.22) * mm, "end": v(6.74, -13.4) * mm});
            skLineSegment(sketch, "E990", {"start": v(6.74, -13.4) * mm, "end": v(6.63, -13.67) * mm});
            skLineSegment(sketch, "E991", {"start": v(6.63, -13.67) * mm, "end": v(6.54, -13.97) * mm});
            skLineSegment(sketch, "E992", {"start": v(6.54, -13.97) * mm, "end": v(6.47, -14.38) * mm});
            skLineSegment(sketch, "E993", {"start": v(6.47, -14.38) * mm, "end": v(6.44, -14.83) * mm});
            skArc(sketch, "E994", {"start": v(6.44, -14.83) * mm, "mid": v(6.72, -15.05) * mm, "end": v(7.01, -15.25) * mm});
            skLineSegment(sketch, "E995", {"start": v(8.76, -13.68) * mm, "end": v(8.64, -13.94) * mm});
            skLineSegment(sketch, "E996", {"start": v(8.64, -13.94) * mm, "end": v(8.54, -14.15) * mm});
            skLineSegment(sketch, "E997", {"start": v(8.54, -14.15) * mm, "end": v(8.48, -14.25) * mm});
            skLineSegment(sketch, "E998", {"start": v(8.48, -14.25) * mm, "end": v(8.46, -14.3) * mm});
            skLineSegment(sketch, "E999", {"start": v(8.46, -14.3) * mm, "end": v(8.42, -14.36) * mm});
            skLineSegment(sketch, "E1000", {"start": v(8.42, -14.36) * mm, "end": v(8.27, -14.53) * mm});
            skLineSegment(sketch, "E1001", {"start": v(8.27, -14.53) * mm, "end": v(8.06, -14.7) * mm});
            skLineSegment(sketch, "E1002", {"start": v(8.06, -14.7) * mm, "end": v(7.8, -14.89) * mm});
            skLineSegment(sketch, "E1003", {"start": v(7.8, -14.89) * mm, "end": v(7.43, -15.08) * mm});
            skLineSegment(sketch, "E1004", {"start": v(7.43, -15.08) * mm, "end": v(7.01, -15.25) * mm});
            skArc(sketch, "E1005", {"start": v(9.38, -13.44) * mm, "mid": v(9.03, -13.44) * mm, "end": v(8.76, -13.68) * mm});
            skArc(sketch, "E1006", {"start": v(9.38, -13.44) * mm, "mid": v(9.56, -13.5) * mm, "end": v(9.75, -13.56) * mm});
            skArc(sketch, "E1007", {"start": v(10.1, -14.12) * mm, "mid": v(10.03, -13.77) * mm, "end": v(9.75, -13.56) * mm});
            skLineSegment(sketch, "E1008", {"start": v(10.1, -14.12) * mm, "end": v(10.05, -14.4) * mm});
            skLineSegment(sketch, "E1009", {"start": v(10.05, -14.4) * mm, "end": v(10.01, -14.63) * mm});
            skLineSegment(sketch, "E1010", {"start": v(10.01, -14.63) * mm, "end": v(10, -14.74) * mm});
            skLineSegment(sketch, "E1011", {"start": v(10, -14.74) * mm, "end": v(9.99, -14.8) * mm});
            skLineSegment(sketch, "E1012", {"start": v(9.99, -14.8) * mm, "end": v(9.98, -14.86) * mm});
            skLineSegment(sketch, "E1013", {"start": v(9.98, -14.86) * mm, "end": v(10, -15.09) * mm});
            skLineSegment(sketch, "E1014", {"start": v(10, -15.09) * mm, "end": v(10.07, -15.36) * mm});
            skLineSegment(sketch, "E1015", {"start": v(10.07, -15.36) * mm, "end": v(10.17, -15.66) * mm});
            skLineSegment(sketch, "E1016", {"start": v(10.17, -15.66) * mm, "end": v(10.36, -16.03) * mm});
            skLineSegment(sketch, "E1017", {"start": v(10.36, -16.03) * mm, "end": v(10.6, -16.41) * mm});
            skArc(sketch, "E1018", {"start": v(10.6, -16.41) * mm, "mid": v(10.95, -16.42) * mm, "end": v(11.3, -16.41) * mm});
            skLineSegment(sketch, "E1019", {"start": v(11.8, -14.12) * mm, "end": v(11.86, -14.4) * mm});
            skLineSegment(sketch, "E1020", {"start": v(11.86, -14.4) * mm, "end": v(11.9, -14.63) * mm});
            skLineSegment(sketch, "E1021", {"start": v(11.9, -14.63) * mm, "end": v(11.91, -14.74) * mm});
            skLineSegment(sketch, "E1022", {"start": v(11.91, -14.74) * mm, "end": v(11.92, -14.8) * mm});
            skLineSegment(sketch, "E1023", {"start": v(11.92, -14.8) * mm, "end": v(11.92, -14.86) * mm});
            skLineSegment(sketch, "E1024", {"start": v(11.92, -14.86) * mm, "end": v(11.9, -15.09) * mm});
            skLineSegment(sketch, "E1025", {"start": v(11.9, -15.09) * mm, "end": v(11.84, -15.36) * mm});
            skLineSegment(sketch, "E1026", {"start": v(11.84, -15.36) * mm, "end": v(11.73, -15.66) * mm});
            skLineSegment(sketch, "E1027", {"start": v(11.73, -15.66) * mm, "end": v(11.55, -16.03) * mm});
            skLineSegment(sketch, "E1028", {"start": v(11.55, -16.03) * mm, "end": v(11.3, -16.41) * mm});
            skSolve(sketch);
        }
        {
            var Q0;
            Q0 = qSketchRegion(id + "F0", true);
            extrude(context, id + "F1", {"entities" : qUnion([Q0]), "depth" : 3 * mm, "offsetDistance" : 25 * mm});
        }
    });
